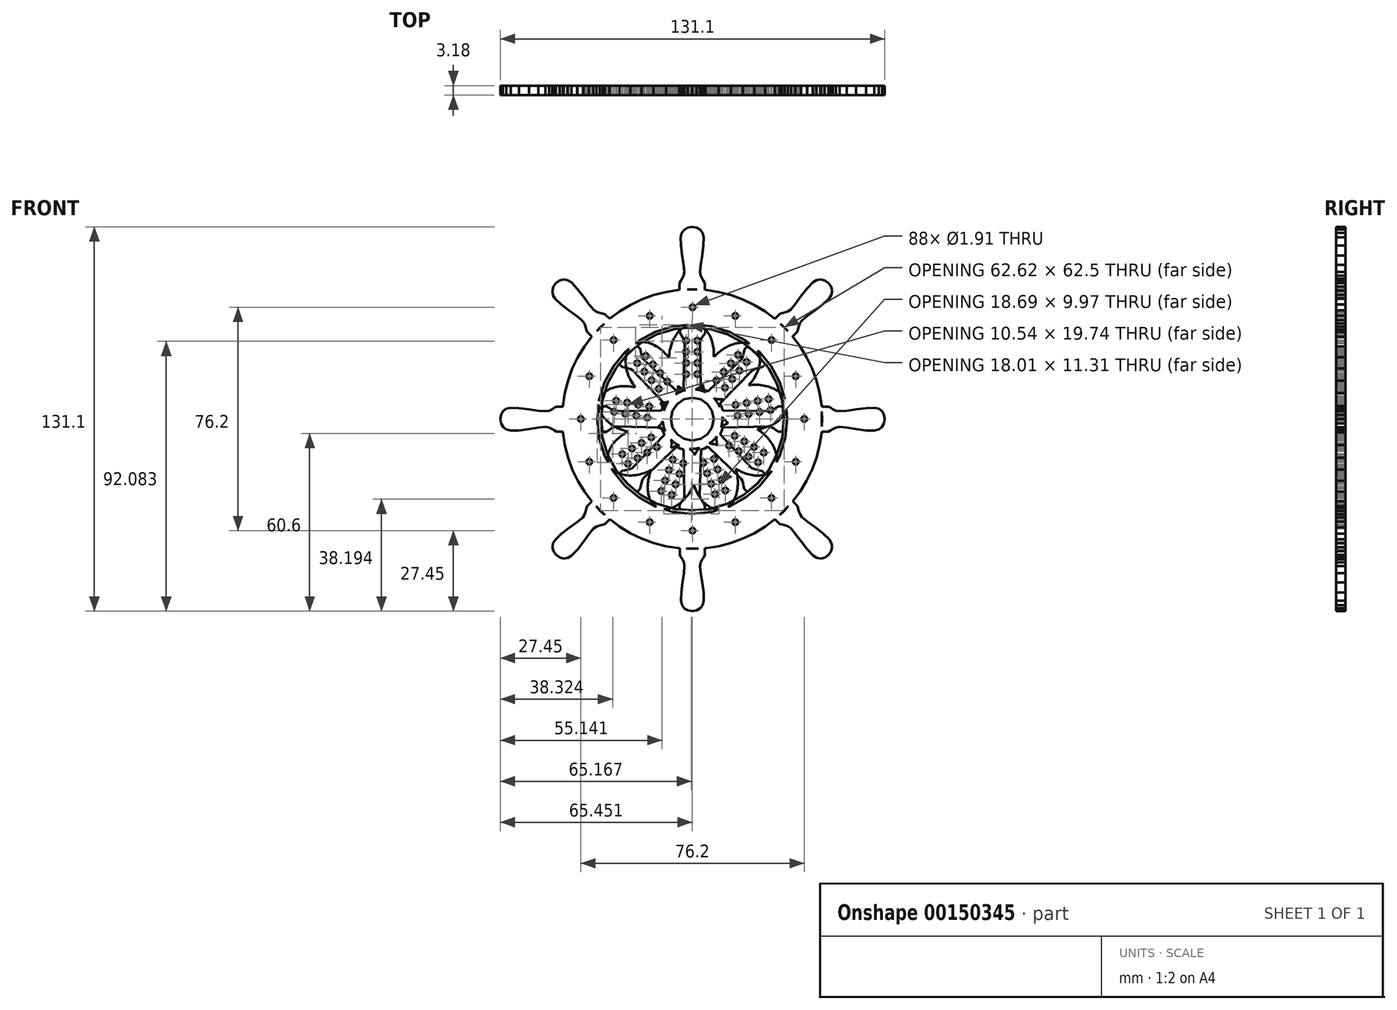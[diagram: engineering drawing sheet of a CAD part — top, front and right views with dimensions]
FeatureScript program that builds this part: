
annotation { "Feature Type Name" : "Feature", "Feature Type Description" : "" }
export const myFeature = defineFeature(function(context is Context, id is Id, definition is map)
    precondition{}
    {
        {
            var Q0;
            Q0=qCreatedBy(makeId("Front.planeOp"),FACE);
            var sketch = newSketch(context, id + "F0", { "sketchPlane" : qUnion([Q0])});
            skLineSegment(sketch, "E0", {"start": v(-9.65, -2.99) * mm, "end": v(-26.1, -2.56) * mm});
            skLineSegment(sketch, "E1", {"start": v(-26.1, -2.56) * mm, "end": v(-26.82, -2.77) * mm});
            skLineSegment(sketch, "E2", {"start": v(-26.82, -2.77) * mm, "end": v(-27.64, -3.22) * mm});
            skLineSegment(sketch, "E3", {"start": v(-27.64, -3.22) * mm, "end": v(-28.5, -3.78) * mm});
            skLineSegment(sketch, "E4", {"start": v(-28.5, -3.78) * mm, "end": v(-29.36, -4.29) * mm});
            skLineSegment(sketch, "E5", {"start": v(-29.36, -4.29) * mm, "end": v(-30.78, -4.29) * mm});
            skLineSegment(sketch, "E6", {"start": v(-30.78, -4.29) * mm, "end": v(-31.08, 0.04) * mm});
            skLineSegment(sketch, "E7", {"start": v(-31.08, 0.04) * mm, "end": v(-30.78, 4.37) * mm});
            skLineSegment(sketch, "E8", {"start": v(-30.78, 4.37) * mm, "end": v(-29.29, 4.37) * mm});
            skLineSegment(sketch, "E9", {"start": v(-29.29, 4.37) * mm, "end": v(-28.5, 3.85) * mm});
            skLineSegment(sketch, "E10", {"start": v(-28.5, 3.85) * mm, "end": v(-27.69, 3.29) * mm});
            skLineSegment(sketch, "E11", {"start": v(-27.69, 3.29) * mm, "end": v(-26.91, 2.84) * mm});
            skLineSegment(sketch, "E12", {"start": v(-26.91, 2.84) * mm, "end": v(-26.22, 2.67) * mm});
            skLineSegment(sketch, "E13", {"start": v(-26.22, 2.67) * mm, "end": v(-9.66, 2.93) * mm});
            skLineSegment(sketch, "E14", {"start": v(-29.33, -4.38) * mm, "end": v(-29.55, 0) * mm});
            skLineSegment(sketch, "E15", {"start": v(-29.55, 0) * mm, "end": v(-29.33, 4.44) * mm});
            skLineSegment(sketch, "E16", {"start": v(-62.02, -3.96) * mm, "end": v(-59.16, -3.9) * mm});
            skLineSegment(sketch, "E17", {"start": v(-59.16, -3.9) * mm, "end": v(-55.76, -3.45) * mm});
            skLineSegment(sketch, "E18", {"start": v(-55.76, -3.45) * mm, "end": v(-52.53, -2.95) * mm});
            skLineSegment(sketch, "E19", {"start": v(-52.53, -2.95) * mm, "end": v(-50.15, -2.7) * mm});
            skLineSegment(sketch, "E20", {"start": v(-50.15, -2.7) * mm, "end": v(-48.91, -2.92) * mm});
            skLineSegment(sketch, "E21", {"start": v(-48.91, -2.92) * mm, "end": v(-47.83, -3.44) * mm});
            skLineSegment(sketch, "E22", {"start": v(-47.83, -3.44) * mm, "end": v(-46.94, -3.98) * mm});
            skLineSegment(sketch, "E23", {"start": v(-46.94, -3.98) * mm, "end": v(-46.3, -4.31) * mm});
            skLineSegment(sketch, "E24", {"start": v(-46.3, -4.31) * mm, "end": v(-44.13, -4.33) * mm});
            skLineSegment(sketch, "E25", {"start": v(-44.13, -4.33) * mm, "end": v(-44.13, 4.25) * mm});
            skLineSegment(sketch, "E26", {"start": v(-44.13, 4.25) * mm, "end": v(-46.3, 4.23) * mm});
            skLineSegment(sketch, "E27", {"start": v(-46.3, 4.23) * mm, "end": v(-46.94, 3.9) * mm});
            skLineSegment(sketch, "E28", {"start": v(-46.94, 3.9) * mm, "end": v(-47.83, 3.36) * mm});
            skLineSegment(sketch, "E29", {"start": v(-47.83, 3.36) * mm, "end": v(-48.91, 2.85) * mm});
            skLineSegment(sketch, "E30", {"start": v(-48.91, 2.85) * mm, "end": v(-50.15, 2.62) * mm});
            skLineSegment(sketch, "E31", {"start": v(-50.15, 2.62) * mm, "end": v(-52.53, 2.85) * mm});
            skLineSegment(sketch, "E32", {"start": v(-52.53, 2.85) * mm, "end": v(-55.75, 3.32) * mm});
            skLineSegment(sketch, "E33", {"start": v(-55.75, 3.32) * mm, "end": v(-59.15, 3.75) * mm});
            skLineSegment(sketch, "E34", {"start": v(-59.15, 3.75) * mm, "end": v(-62.02, 3.87) * mm});
            skLineSegment(sketch, "E35", {"start": v(-62.02, 3.87) * mm, "end": v(-63.52, 3.5) * mm});
            skLineSegment(sketch, "E36", {"start": v(-63.52, 3.5) * mm, "end": v(-64.63, 2.66) * mm});
            skLineSegment(sketch, "E37", {"start": v(-64.63, 2.66) * mm, "end": v(-65.32, 1.44) * mm});
            skLineSegment(sketch, "E38", {"start": v(-65.32, 1.44) * mm, "end": v(-65.55, -0.04) * mm});
            skLineSegment(sketch, "E39", {"start": v(-65.55, -0.04) * mm, "end": v(-65.3, -1.56) * mm});
            skLineSegment(sketch, "E40", {"start": v(-65.3, -1.56) * mm, "end": v(-64.57, -2.76) * mm});
            skLineSegment(sketch, "E41", {"start": v(-64.57, -2.76) * mm, "end": v(-63.45, -3.57) * mm});
            skLineSegment(sketch, "E42", {"start": v(-63.45, -3.57) * mm, "end": v(-62.02, -3.96) * mm});
            skLineSegment(sketch, "E43", {"start": v(-46.16, -4.38) * mm, "end": v(-46.53, -0.02) * mm});
            skLineSegment(sketch, "E44", {"start": v(-46.53, -0.02) * mm, "end": v(-46.16, 4.33) * mm});
            skLineSegment(sketch, "E45", {"start": v(2.89, -9.76) * mm, "end": v(2.46, -26.18) * mm});
            skLineSegment(sketch, "E46", {"start": v(2.46, -26.18) * mm, "end": v(2.67, -26.9) * mm});
            skLineSegment(sketch, "E47", {"start": v(2.67, -26.9) * mm, "end": v(3.12, -27.72) * mm});
            skLineSegment(sketch, "E48", {"start": v(3.12, -27.72) * mm, "end": v(3.68, -28.58) * mm});
            skLineSegment(sketch, "E49", {"start": v(3.68, -28.58) * mm, "end": v(4.19, -29.44) * mm});
            skLineSegment(sketch, "E50", {"start": v(4.19, -29.44) * mm, "end": v(4.19, -30.85) * mm});
            skLineSegment(sketch, "E51", {"start": v(4.19, -30.85) * mm, "end": v(-0.15, -31.15) * mm});
            skLineSegment(sketch, "E52", {"start": v(-0.15, -31.15) * mm, "end": v(-4.49, -30.85) * mm});
            skLineSegment(sketch, "E53", {"start": v(-4.49, -30.85) * mm, "end": v(-4.49, -29.36) * mm});
            skLineSegment(sketch, "E54", {"start": v(-4.49, -29.36) * mm, "end": v(-3.97, -28.57) * mm});
            skLineSegment(sketch, "E55", {"start": v(-3.97, -28.57) * mm, "end": v(-3.4, -27.76) * mm});
            skLineSegment(sketch, "E56", {"start": v(-3.4, -27.76) * mm, "end": v(-2.96, -27) * mm});
            skLineSegment(sketch, "E57", {"start": v(-2.96, -27) * mm, "end": v(-2.79, -26.3) * mm});
            skLineSegment(sketch, "E58", {"start": v(-2.79, -26.3) * mm, "end": v(-3.05, -9.77) * mm});
            skLineSegment(sketch, "E59", {"start": v(4.28, -29.4) * mm, "end": v(-0.1, -29.62) * mm});
            skLineSegment(sketch, "E60", {"start": v(-0.1, -29.62) * mm, "end": v(-4.56, -29.4) * mm});
            skLineSegment(sketch, "E61", {"start": v(3.86, -62.02) * mm, "end": v(3.79, -59.17) * mm});
            skLineSegment(sketch, "E62", {"start": v(3.79, -59.17) * mm, "end": v(3.34, -55.78) * mm});
            skLineSegment(sketch, "E63", {"start": v(3.34, -55.78) * mm, "end": v(2.84, -52.55) * mm});
            skLineSegment(sketch, "E64", {"start": v(2.84, -52.55) * mm, "end": v(2.6, -50.18) * mm});
            skLineSegment(sketch, "E65", {"start": v(2.6, -50.18) * mm, "end": v(2.82, -48.95) * mm});
            skLineSegment(sketch, "E66", {"start": v(2.82, -48.95) * mm, "end": v(3.33, -47.86) * mm});
            skLineSegment(sketch, "E67", {"start": v(3.33, -47.86) * mm, "end": v(3.88, -46.98) * mm});
            skLineSegment(sketch, "E68", {"start": v(3.88, -46.98) * mm, "end": v(4.21, -46.34) * mm});
            skLineSegment(sketch, "E69", {"start": v(4.21, -46.34) * mm, "end": v(4.23, -44.17) * mm});
            skLineSegment(sketch, "E70", {"start": v(4.23, -44.17) * mm, "end": v(-4.37, -44.17) * mm});
            skLineSegment(sketch, "E71", {"start": v(-4.37, -44.17) * mm, "end": v(-4.35, -46.34) * mm});
            skLineSegment(sketch, "E72", {"start": v(-4.35, -46.34) * mm, "end": v(-4.02, -46.98) * mm});
            skLineSegment(sketch, "E73", {"start": v(-4.02, -46.98) * mm, "end": v(-3.48, -47.86) * mm});
            skLineSegment(sketch, "E74", {"start": v(-3.48, -47.86) * mm, "end": v(-2.96, -48.95) * mm});
            skLineSegment(sketch, "E75", {"start": v(-2.96, -48.95) * mm, "end": v(-2.74, -50.18) * mm});
            skLineSegment(sketch, "E76", {"start": v(-2.74, -50.18) * mm, "end": v(-2.97, -52.55) * mm});
            skLineSegment(sketch, "E77", {"start": v(-2.97, -52.55) * mm, "end": v(-3.44, -55.77) * mm});
            skLineSegment(sketch, "E78", {"start": v(-3.44, -55.77) * mm, "end": v(-3.87, -59.16) * mm});
            skLineSegment(sketch, "E79", {"start": v(-3.87, -59.16) * mm, "end": v(-3.99, -62.02) * mm});
            skLineSegment(sketch, "E80", {"start": v(-3.99, -62.02) * mm, "end": v(-3.62, -63.52) * mm});
            skLineSegment(sketch, "E81", {"start": v(-3.62, -63.52) * mm, "end": v(-2.77, -64.63) * mm});
            skLineSegment(sketch, "E82", {"start": v(-2.77, -64.63) * mm, "end": v(-1.55, -65.31) * mm});
            skLineSegment(sketch, "E83", {"start": v(-1.55, -65.31) * mm, "end": v(-0.07, -65.55) * mm});
            skLineSegment(sketch, "E84", {"start": v(-0.07, -65.55) * mm, "end": v(1.46, -65.3) * mm});
            skLineSegment(sketch, "E85", {"start": v(1.46, -65.3) * mm, "end": v(2.65, -64.57) * mm});
            skLineSegment(sketch, "E86", {"start": v(2.65, -64.57) * mm, "end": v(3.47, -63.46) * mm});
            skLineSegment(sketch, "E87", {"start": v(3.47, -63.46) * mm, "end": v(3.86, -62.02) * mm});
            skLineSegment(sketch, "E88", {"start": v(4.27, -46.2) * mm, "end": v(-0.09, -46.56) * mm});
            skLineSegment(sketch, "E89", {"start": v(-0.09, -46.56) * mm, "end": v(-4.45, -46.2) * mm});
            skLineSegment(sketch, "E90", {"start": v(-3.08, 9.76) * mm, "end": v(-2.66, 26.18) * mm});
            skLineSegment(sketch, "E91", {"start": v(-2.66, 26.18) * mm, "end": v(-2.86, 26.9) * mm});
            skLineSegment(sketch, "E92", {"start": v(-2.86, 26.9) * mm, "end": v(-3.32, 27.72) * mm});
            skLineSegment(sketch, "E93", {"start": v(-3.32, 27.72) * mm, "end": v(-3.88, 28.58) * mm});
            skLineSegment(sketch, "E94", {"start": v(-3.88, 28.58) * mm, "end": v(-4.38, 29.44) * mm});
            skLineSegment(sketch, "E95", {"start": v(-4.38, 29.44) * mm, "end": v(-4.38, 30.85) * mm});
            skLineSegment(sketch, "E96", {"start": v(-4.38, 30.85) * mm, "end": v(-0.05, 31.15) * mm});
            skLineSegment(sketch, "E97", {"start": v(-0.05, 31.15) * mm, "end": v(4.29, 30.85) * mm});
            skLineSegment(sketch, "E98", {"start": v(4.29, 30.85) * mm, "end": v(4.29, 29.36) * mm});
            skLineSegment(sketch, "E99", {"start": v(4.29, 29.36) * mm, "end": v(3.77, 28.57) * mm});
            skLineSegment(sketch, "E100", {"start": v(3.77, 28.57) * mm, "end": v(3.2, 27.76) * mm});
            skLineSegment(sketch, "E101", {"start": v(3.2, 27.76) * mm, "end": v(2.76, 27) * mm});
            skLineSegment(sketch, "E102", {"start": v(2.76, 27) * mm, "end": v(2.59, 26.3) * mm});
            skLineSegment(sketch, "E103", {"start": v(2.59, 26.3) * mm, "end": v(2.85, 9.77) * mm});
            skLineSegment(sketch, "E104", {"start": v(-4.48, 29.4) * mm, "end": v(-0.1, 29.62) * mm});
            skLineSegment(sketch, "E105", {"start": v(-0.1, 29.62) * mm, "end": v(4.36, 29.4) * mm});
            skLineSegment(sketch, "E106", {"start": v(-4.05, 62.02) * mm, "end": v(-3.99, 59.17) * mm});
            skLineSegment(sketch, "E107", {"start": v(-3.99, 59.17) * mm, "end": v(-3.54, 55.78) * mm});
            skLineSegment(sketch, "E108", {"start": v(-3.54, 55.78) * mm, "end": v(-3.04, 52.56) * mm});
            skLineSegment(sketch, "E109", {"start": v(-3.04, 52.56) * mm, "end": v(-2.8, 50.18) * mm});
            skLineSegment(sketch, "E110", {"start": v(-2.8, 50.18) * mm, "end": v(-3.02, 48.95) * mm});
            skLineSegment(sketch, "E111", {"start": v(-3.02, 48.95) * mm, "end": v(-3.53, 47.86) * mm});
            skLineSegment(sketch, "E112", {"start": v(-3.53, 47.86) * mm, "end": v(-4.08, 46.98) * mm});
            skLineSegment(sketch, "E113", {"start": v(-4.08, 46.98) * mm, "end": v(-4.4, 46.34) * mm});
            skLineSegment(sketch, "E114", {"start": v(-4.4, 46.34) * mm, "end": v(-4.43, 44.17) * mm});
            skLineSegment(sketch, "E115", {"start": v(-4.43, 44.17) * mm, "end": v(4.17, 44.17) * mm});
            skLineSegment(sketch, "E116", {"start": v(4.17, 44.17) * mm, "end": v(4.15, 46.34) * mm});
            skLineSegment(sketch, "E117", {"start": v(4.15, 46.34) * mm, "end": v(3.82, 46.98) * mm});
            skLineSegment(sketch, "E118", {"start": v(3.82, 46.98) * mm, "end": v(3.28, 47.86) * mm});
            skLineSegment(sketch, "E119", {"start": v(3.28, 47.86) * mm, "end": v(2.76, 48.95) * mm});
            skLineSegment(sketch, "E120", {"start": v(2.76, 48.95) * mm, "end": v(2.54, 50.18) * mm});
            skLineSegment(sketch, "E121", {"start": v(2.54, 50.18) * mm, "end": v(2.77, 52.55) * mm});
            skLineSegment(sketch, "E122", {"start": v(2.77, 52.55) * mm, "end": v(3.24, 55.77) * mm});
            skLineSegment(sketch, "E123", {"start": v(3.24, 55.77) * mm, "end": v(3.67, 59.16) * mm});
            skLineSegment(sketch, "E124", {"start": v(3.67, 59.16) * mm, "end": v(3.8, 62.02) * mm});
            skLineSegment(sketch, "E125", {"start": v(3.8, 62.02) * mm, "end": v(3.42, 63.52) * mm});
            skLineSegment(sketch, "E126", {"start": v(3.42, 63.52) * mm, "end": v(2.57, 64.63) * mm});
            skLineSegment(sketch, "E127", {"start": v(2.57, 64.63) * mm, "end": v(1.35, 65.32) * mm});
            skLineSegment(sketch, "E128", {"start": v(1.35, 65.32) * mm, "end": v(-0.13, 65.55) * mm});
            skLineSegment(sketch, "E129", {"start": v(-0.13, 65.55) * mm, "end": v(-1.65, 65.3) * mm});
            skLineSegment(sketch, "E130", {"start": v(-1.65, 65.3) * mm, "end": v(-2.85, 64.57) * mm});
            skLineSegment(sketch, "E131", {"start": v(-2.85, 64.57) * mm, "end": v(-3.67, 63.46) * mm});
            skLineSegment(sketch, "E132", {"start": v(-3.67, 63.46) * mm, "end": v(-4.05, 62.02) * mm});
            skLineSegment(sketch, "E133", {"start": v(-4.47, 46.2) * mm, "end": v(-0.11, 46.57) * mm});
            skLineSegment(sketch, "E134", {"start": v(-0.11, 46.57) * mm, "end": v(4.25, 46.2) * mm});
            skLineSegment(sketch, "E135", {"start": v(8.93, -4.8) * mm, "end": v(20.26, -16.7) * mm});
            skLineSegment(sketch, "E136", {"start": v(20.26, -16.7) * mm, "end": v(20.92, -17.07) * mm});
            skLineSegment(sketch, "E137", {"start": v(20.92, -17.07) * mm, "end": v(21.82, -17.33) * mm});
            skLineSegment(sketch, "E138", {"start": v(21.82, -17.33) * mm, "end": v(22.82, -17.54) * mm});
            skLineSegment(sketch, "E139", {"start": v(22.82, -17.54) * mm, "end": v(23.79, -17.8) * mm});
            skLineSegment(sketch, "E140", {"start": v(23.79, -17.8) * mm, "end": v(24.79, -18.79) * mm});
            skLineSegment(sketch, "E141", {"start": v(24.79, -18.79) * mm, "end": v(21.94, -22.07) * mm});
            skLineSegment(sketch, "E142", {"start": v(21.94, -22.07) * mm, "end": v(18.65, -24.9) * mm});
            skLineSegment(sketch, "E143", {"start": v(18.65, -24.9) * mm, "end": v(17.6, -23.86) * mm});
            skLineSegment(sketch, "E144", {"start": v(17.6, -23.86) * mm, "end": v(17.4, -22.93) * mm});
            skLineSegment(sketch, "E145", {"start": v(17.4, -22.93) * mm, "end": v(17.24, -21.96) * mm});
            skLineSegment(sketch, "E146", {"start": v(17.24, -21.96) * mm, "end": v(17, -21.1) * mm});
            skLineSegment(sketch, "E147", {"start": v(17, -21.1) * mm, "end": v(16.63, -20.5) * mm});
            skLineSegment(sketch, "E148", {"start": v(16.63, -20.5) * mm, "end": v(4.74, -9) * mm});
            skLineSegment(sketch, "E149", {"start": v(23.83, -17.7) * mm, "end": v(20.88, -20.95) * mm});
            skLineSegment(sketch, "E150", {"start": v(20.88, -20.95) * mm, "end": v(17.58, -23.94) * mm});
            skLineSegment(sketch, "E151", {"start": v(46.64, -41.07) * mm, "end": v(44.57, -39.1) * mm});
            skLineSegment(sketch, "E152", {"start": v(44.57, -39.1) * mm, "end": v(41.86, -37.01) * mm});
            skLineSegment(sketch, "E153", {"start": v(41.86, -37.01) * mm, "end": v(39.22, -35.08) * mm});
            skLineSegment(sketch, "E154", {"start": v(39.22, -35.08) * mm, "end": v(37.36, -33.58) * mm});
            skLineSegment(sketch, "E155", {"start": v(37.36, -33.58) * mm, "end": v(36.65, -32.55) * mm});
            skLineSegment(sketch, "E156", {"start": v(36.65, -32.55) * mm, "end": v(36.24, -31.42) * mm});
            skLineSegment(sketch, "E157", {"start": v(36.24, -31.42) * mm, "end": v(36, -30.4) * mm});
            skLineSegment(sketch, "E158", {"start": v(36, -30.4) * mm, "end": v(35.78, -29.73) * mm});
            skLineSegment(sketch, "E159", {"start": v(35.78, -29.73) * mm, "end": v(34.26, -28.18) * mm});
            skLineSegment(sketch, "E160", {"start": v(34.26, -28.18) * mm, "end": v(28.18, -34.25) * mm});
            skLineSegment(sketch, "E161", {"start": v(28.18, -34.25) * mm, "end": v(29.73, -35.77) * mm});
            skLineSegment(sketch, "E162", {"start": v(29.73, -35.77) * mm, "end": v(30.41, -35.99) * mm});
            skLineSegment(sketch, "E163", {"start": v(30.41, -35.99) * mm, "end": v(31.43, -36.23) * mm});
            skLineSegment(sketch, "E164", {"start": v(31.43, -36.23) * mm, "end": v(32.56, -36.63) * mm});
            skLineSegment(sketch, "E165", {"start": v(32.56, -36.63) * mm, "end": v(33.59, -37.35) * mm});
            skLineSegment(sketch, "E166", {"start": v(33.59, -37.35) * mm, "end": v(35.1, -39.18) * mm});
            skLineSegment(sketch, "E167", {"start": v(35.1, -39.18) * mm, "end": v(37.06, -41.8) * mm});
            skLineSegment(sketch, "E168", {"start": v(37.06, -41.8) * mm, "end": v(39.15, -44.5) * mm});
            skLineSegment(sketch, "E169", {"start": v(39.15, -44.5) * mm, "end": v(41.1, -46.6) * mm});
            skLineSegment(sketch, "E170", {"start": v(41.1, -46.6) * mm, "end": v(42.42, -47.4) * mm});
            skLineSegment(sketch, "E171", {"start": v(42.42, -47.4) * mm, "end": v(43.8, -47.58) * mm});
            skLineSegment(sketch, "E172", {"start": v(43.8, -47.58) * mm, "end": v(45.15, -47.2) * mm});
            skLineSegment(sketch, "E173", {"start": v(45.15, -47.2) * mm, "end": v(46.37, -46.33) * mm});
            skLineSegment(sketch, "E174", {"start": v(46.37, -46.33) * mm, "end": v(47.26, -45.07) * mm});
            skLineSegment(sketch, "E175", {"start": v(47.26, -45.07) * mm, "end": v(47.6, -43.72) * mm});
            skLineSegment(sketch, "E176", {"start": v(47.6, -43.72) * mm, "end": v(47.39, -42.35) * mm});
            skLineSegment(sketch, "E177", {"start": v(47.39, -42.35) * mm, "end": v(46.64, -41.07) * mm});
            skLineSegment(sketch, "E178", {"start": v(35.73, -29.58) * mm, "end": v(32.9, -32.92) * mm});
            skLineSegment(sketch, "E179", {"start": v(32.9, -32.92) * mm, "end": v(29.56, -35.74) * mm});
            skLineSegment(sketch, "E180", {"start": v(-9.13, 4.8) * mm, "end": v(-20.46, 16.7) * mm});
            skLineSegment(sketch, "E181", {"start": v(-20.46, 16.7) * mm, "end": v(-21.12, 17.07) * mm});
            skLineSegment(sketch, "E182", {"start": v(-21.12, 17.07) * mm, "end": v(-22.02, 17.33) * mm});
            skLineSegment(sketch, "E183", {"start": v(-22.02, 17.33) * mm, "end": v(-23.02, 17.55) * mm});
            skLineSegment(sketch, "E184", {"start": v(-23.02, 17.55) * mm, "end": v(-23.98, 17.8) * mm});
            skLineSegment(sketch, "E185", {"start": v(-23.98, 17.8) * mm, "end": v(-24.98, 18.79) * mm});
            skLineSegment(sketch, "E186", {"start": v(-24.98, 18.79) * mm, "end": v(-22.14, 22.07) * mm});
            skLineSegment(sketch, "E187", {"start": v(-22.14, 22.07) * mm, "end": v(-18.85, 24.9) * mm});
            skLineSegment(sketch, "E188", {"start": v(-18.85, 24.9) * mm, "end": v(-17.8, 23.86) * mm});
            skLineSegment(sketch, "E189", {"start": v(-17.8, 23.86) * mm, "end": v(-17.6, 22.93) * mm});
            skLineSegment(sketch, "E190", {"start": v(-17.6, 22.93) * mm, "end": v(-17.43, 21.97) * mm});
            skLineSegment(sketch, "E191", {"start": v(-17.43, 21.97) * mm, "end": v(-17.2, 21.1) * mm});
            skLineSegment(sketch, "E192", {"start": v(-17.2, 21.1) * mm, "end": v(-16.83, 20.5) * mm});
            skLineSegment(sketch, "E193", {"start": v(-16.83, 20.5) * mm, "end": v(-4.94, 9) * mm});
            skLineSegment(sketch, "E194", {"start": v(-24.03, 17.7) * mm, "end": v(-21.08, 20.95) * mm});
            skLineSegment(sketch, "E195", {"start": v(-21.08, 20.95) * mm, "end": v(-17.78, 23.94) * mm});
            skLineSegment(sketch, "E196", {"start": v(-46.84, 41.07) * mm, "end": v(-44.77, 39.1) * mm});
            skLineSegment(sketch, "E197", {"start": v(-44.77, 39.1) * mm, "end": v(-42.06, 37.01) * mm});
            skLineSegment(sketch, "E198", {"start": v(-42.06, 37.01) * mm, "end": v(-39.42, 35.09) * mm});
            skLineSegment(sketch, "E199", {"start": v(-39.42, 35.09) * mm, "end": v(-37.56, 33.58) * mm});
            skLineSegment(sketch, "E200", {"start": v(-37.56, 33.58) * mm, "end": v(-36.84, 32.55) * mm});
            skLineSegment(sketch, "E201", {"start": v(-36.84, 32.55) * mm, "end": v(-36.44, 31.42) * mm});
            skLineSegment(sketch, "E202", {"start": v(-36.44, 31.42) * mm, "end": v(-36.2, 30.4) * mm});
            skLineSegment(sketch, "E203", {"start": v(-36.2, 30.4) * mm, "end": v(-35.98, 29.73) * mm});
            skLineSegment(sketch, "E204", {"start": v(-35.98, 29.73) * mm, "end": v(-34.45, 28.18) * mm});
            skLineSegment(sketch, "E205", {"start": v(-34.45, 28.18) * mm, "end": v(-28.38, 34.25) * mm});
            skLineSegment(sketch, "E206", {"start": v(-28.38, 34.25) * mm, "end": v(-29.93, 35.77) * mm});
            skLineSegment(sketch, "E207", {"start": v(-29.93, 35.77) * mm, "end": v(-30.61, 35.99) * mm});
            skLineSegment(sketch, "E208", {"start": v(-30.61, 35.99) * mm, "end": v(-31.62, 36.23) * mm});
            skLineSegment(sketch, "E209", {"start": v(-31.62, 36.23) * mm, "end": v(-32.76, 36.63) * mm});
            skLineSegment(sketch, "E210", {"start": v(-32.76, 36.63) * mm, "end": v(-33.79, 37.35) * mm});
            skLineSegment(sketch, "E211", {"start": v(-33.79, 37.35) * mm, "end": v(-35.3, 39.18) * mm});
            skLineSegment(sketch, "E212", {"start": v(-35.3, 39.18) * mm, "end": v(-37.26, 41.8) * mm});
            skLineSegment(sketch, "E213", {"start": v(-37.26, 41.8) * mm, "end": v(-39.35, 44.5) * mm});
            skLineSegment(sketch, "E214", {"start": v(-39.35, 44.5) * mm, "end": v(-41.3, 46.6) * mm});
            skLineSegment(sketch, "E215", {"start": v(-41.3, 46.6) * mm, "end": v(-42.62, 47.4) * mm});
            skLineSegment(sketch, "E216", {"start": v(-42.62, 47.4) * mm, "end": v(-44, 47.59) * mm});
            skLineSegment(sketch, "E217", {"start": v(-44, 47.59) * mm, "end": v(-45.35, 47.21) * mm});
            skLineSegment(sketch, "E218", {"start": v(-45.35, 47.21) * mm, "end": v(-46.57, 46.33) * mm});
            skLineSegment(sketch, "E219", {"start": v(-46.57, 46.33) * mm, "end": v(-47.46, 45.07) * mm});
            skLineSegment(sketch, "E220", {"start": v(-47.46, 45.07) * mm, "end": v(-47.8, 43.72) * mm});
            skLineSegment(sketch, "E221", {"start": v(-47.8, 43.72) * mm, "end": v(-47.58, 42.35) * mm});
            skLineSegment(sketch, "E222", {"start": v(-47.58, 42.35) * mm, "end": v(-46.84, 41.07) * mm});
            skLineSegment(sketch, "E223", {"start": v(-35.92, 29.58) * mm, "end": v(-33.1, 32.92) * mm});
            skLineSegment(sketch, "E224", {"start": v(-33.1, 32.92) * mm, "end": v(-29.76, 35.74) * mm});
            skLineSegment(sketch, "E225", {"start": v(-4.9, -9) * mm, "end": v(-16.84, -20.32) * mm});
            skLineSegment(sketch, "E226", {"start": v(-16.84, -20.32) * mm, "end": v(-17.2, -20.97) * mm});
            skLineSegment(sketch, "E227", {"start": v(-17.2, -20.97) * mm, "end": v(-17.46, -21.87) * mm});
            skLineSegment(sketch, "E228", {"start": v(-17.46, -21.87) * mm, "end": v(-17.68, -22.88) * mm});
            skLineSegment(sketch, "E229", {"start": v(-17.68, -22.88) * mm, "end": v(-17.93, -23.84) * mm});
            skLineSegment(sketch, "E230", {"start": v(-17.93, -23.84) * mm, "end": v(-18.93, -24.83) * mm});
            skLineSegment(sketch, "E231", {"start": v(-18.93, -24.83) * mm, "end": v(-22.2, -22) * mm});
            skLineSegment(sketch, "E232", {"start": v(-22.2, -22) * mm, "end": v(-25.06, -18.72) * mm});
            skLineSegment(sketch, "E233", {"start": v(-25.06, -18.72) * mm, "end": v(-24, -17.66) * mm});
            skLineSegment(sketch, "E234", {"start": v(-24, -17.66) * mm, "end": v(-23.08, -17.47) * mm});
            skLineSegment(sketch, "E235", {"start": v(-23.08, -17.47) * mm, "end": v(-22.1, -17.3) * mm});
            skLineSegment(sketch, "E236", {"start": v(-22.1, -17.3) * mm, "end": v(-21.24, -17.07) * mm});
            skLineSegment(sketch, "E237", {"start": v(-21.24, -17.07) * mm, "end": v(-20.63, -16.7) * mm});
            skLineSegment(sketch, "E238", {"start": v(-20.63, -16.7) * mm, "end": v(-9.1, -4.83) * mm});
            skLineSegment(sketch, "E239", {"start": v(-17.84, -23.88) * mm, "end": v(-21.09, -20.94) * mm});
            skLineSegment(sketch, "E240", {"start": v(-21.09, -20.94) * mm, "end": v(-24.09, -17.65) * mm});
            skLineSegment(sketch, "E241", {"start": v(-41.25, -46.65) * mm, "end": v(-39.27, -44.58) * mm});
            skLineSegment(sketch, "E242", {"start": v(-39.27, -44.58) * mm, "end": v(-37.19, -41.87) * mm});
            skLineSegment(sketch, "E243", {"start": v(-37.19, -41.87) * mm, "end": v(-35.26, -39.24) * mm});
            skLineSegment(sketch, "E244", {"start": v(-35.26, -39.24) * mm, "end": v(-33.75, -37.39) * mm});
            skLineSegment(sketch, "E245", {"start": v(-33.75, -37.39) * mm, "end": v(-32.72, -36.67) * mm});
            skLineSegment(sketch, "E246", {"start": v(-32.72, -36.67) * mm, "end": v(-31.58, -36.27) * mm});
            skLineSegment(sketch, "E247", {"start": v(-31.58, -36.27) * mm, "end": v(-30.57, -36.03) * mm});
            skLineSegment(sketch, "E248", {"start": v(-30.57, -36.03) * mm, "end": v(-29.89, -35.81) * mm});
            skLineSegment(sketch, "E249", {"start": v(-29.89, -35.81) * mm, "end": v(-28.34, -34.29) * mm});
            skLineSegment(sketch, "E250", {"start": v(-28.34, -34.29) * mm, "end": v(-34.41, -28.22) * mm});
            skLineSegment(sketch, "E251", {"start": v(-34.41, -28.22) * mm, "end": v(-35.94, -29.77) * mm});
            skLineSegment(sketch, "E252", {"start": v(-35.94, -29.77) * mm, "end": v(-36.16, -30.45) * mm});
            skLineSegment(sketch, "E253", {"start": v(-36.16, -30.45) * mm, "end": v(-36.4, -31.46) * mm});
            skLineSegment(sketch, "E254", {"start": v(-36.4, -31.46) * mm, "end": v(-36.8, -32.6) * mm});
            skLineSegment(sketch, "E255", {"start": v(-36.8, -32.6) * mm, "end": v(-37.52, -33.62) * mm});
            skLineSegment(sketch, "E256", {"start": v(-37.52, -33.62) * mm, "end": v(-39.36, -35.14) * mm});
            skLineSegment(sketch, "E257", {"start": v(-39.36, -35.14) * mm, "end": v(-41.97, -37.08) * mm});
            skLineSegment(sketch, "E258", {"start": v(-41.97, -37.08) * mm, "end": v(-44.68, -39.17) * mm});
            skLineSegment(sketch, "E259", {"start": v(-44.68, -39.17) * mm, "end": v(-46.8, -41.11) * mm});
            skLineSegment(sketch, "E260", {"start": v(-46.8, -41.11) * mm, "end": v(-47.6, -42.43) * mm});
            skLineSegment(sketch, "E261", {"start": v(-47.6, -42.43) * mm, "end": v(-47.78, -43.81) * mm});
            skLineSegment(sketch, "E262", {"start": v(-47.78, -43.81) * mm, "end": v(-47.4, -45.16) * mm});
            skLineSegment(sketch, "E263", {"start": v(-47.4, -45.16) * mm, "end": v(-46.52, -46.37) * mm});
            skLineSegment(sketch, "E264", {"start": v(-46.52, -46.37) * mm, "end": v(-45.26, -47.27) * mm});
            skLineSegment(sketch, "E265", {"start": v(-45.26, -47.27) * mm, "end": v(-43.9, -47.6) * mm});
            skLineSegment(sketch, "E266", {"start": v(-43.9, -47.6) * mm, "end": v(-42.54, -47.39) * mm});
            skLineSegment(sketch, "E267", {"start": v(-42.54, -47.39) * mm, "end": v(-41.25, -46.65) * mm});
            skLineSegment(sketch, "E268", {"start": v(-29.74, -35.75) * mm, "end": v(-33.08, -32.93) * mm});
            skLineSegment(sketch, "E269", {"start": v(-33.08, -32.93) * mm, "end": v(-35.9, -29.6) * mm});
            skLineSegment(sketch, "E270", {"start": v(4.7, 9) * mm, "end": v(16.64, 20.32) * mm});
            skLineSegment(sketch, "E271", {"start": v(16.64, 20.32) * mm, "end": v(17, 20.97) * mm});
            skLineSegment(sketch, "E272", {"start": v(17, 20.97) * mm, "end": v(17.26, 21.88) * mm});
            skLineSegment(sketch, "E273", {"start": v(17.26, 21.88) * mm, "end": v(17.48, 22.88) * mm});
            skLineSegment(sketch, "E274", {"start": v(17.48, 22.88) * mm, "end": v(17.73, 23.84) * mm});
            skLineSegment(sketch, "E275", {"start": v(17.73, 23.84) * mm, "end": v(18.73, 24.84) * mm});
            skLineSegment(sketch, "E276", {"start": v(18.73, 24.84) * mm, "end": v(22.01, 22) * mm});
            skLineSegment(sketch, "E277", {"start": v(22.01, 22) * mm, "end": v(24.86, 18.72) * mm});
            skLineSegment(sketch, "E278", {"start": v(24.86, 18.72) * mm, "end": v(23.8, 17.66) * mm});
            skLineSegment(sketch, "E279", {"start": v(23.8, 17.66) * mm, "end": v(22.88, 17.47) * mm});
            skLineSegment(sketch, "E280", {"start": v(22.88, 17.47) * mm, "end": v(21.9, 17.3) * mm});
            skLineSegment(sketch, "E281", {"start": v(21.9, 17.3) * mm, "end": v(21.04, 17.07) * mm});
            skLineSegment(sketch, "E282", {"start": v(21.04, 17.07) * mm, "end": v(20.43, 16.7) * mm});
            skLineSegment(sketch, "E283", {"start": v(20.43, 16.7) * mm, "end": v(8.91, 4.83) * mm});
            skLineSegment(sketch, "E284", {"start": v(17.64, 23.88) * mm, "end": v(20.89, 20.94) * mm});
            skLineSegment(sketch, "E285", {"start": v(20.89, 20.94) * mm, "end": v(23.9, 17.65) * mm});
            skLineSegment(sketch, "E286", {"start": v(41.05, 46.65) * mm, "end": v(39.07, 44.58) * mm});
            skLineSegment(sketch, "E287", {"start": v(39.07, 44.58) * mm, "end": v(36.99, 41.87) * mm});
            skLineSegment(sketch, "E288", {"start": v(36.99, 41.87) * mm, "end": v(35.06, 39.24) * mm});
            skLineSegment(sketch, "E289", {"start": v(35.06, 39.24) * mm, "end": v(33.55, 37.39) * mm});
            skLineSegment(sketch, "E290", {"start": v(33.55, 37.39) * mm, "end": v(32.52, 36.67) * mm});
            skLineSegment(sketch, "E291", {"start": v(32.52, 36.67) * mm, "end": v(31.39, 36.27) * mm});
            skLineSegment(sketch, "E292", {"start": v(31.39, 36.27) * mm, "end": v(30.37, 36.03) * mm});
            skLineSegment(sketch, "E293", {"start": v(30.37, 36.03) * mm, "end": v(29.69, 35.81) * mm});
            skLineSegment(sketch, "E294", {"start": v(29.69, 35.81) * mm, "end": v(28.14, 34.29) * mm});
            skLineSegment(sketch, "E295", {"start": v(28.14, 34.29) * mm, "end": v(34.22, 28.22) * mm});
            skLineSegment(sketch, "E296", {"start": v(34.22, 28.22) * mm, "end": v(35.74, 29.77) * mm});
            skLineSegment(sketch, "E297", {"start": v(35.74, 29.77) * mm, "end": v(35.96, 30.45) * mm});
            skLineSegment(sketch, "E298", {"start": v(35.96, 30.45) * mm, "end": v(36.2, 31.46) * mm});
            skLineSegment(sketch, "E299", {"start": v(36.2, 31.46) * mm, "end": v(36.6, 32.6) * mm});
            skLineSegment(sketch, "E300", {"start": v(36.6, 32.6) * mm, "end": v(37.32, 33.62) * mm});
            skLineSegment(sketch, "E301", {"start": v(37.32, 33.62) * mm, "end": v(39.16, 35.14) * mm});
            skLineSegment(sketch, "E302", {"start": v(39.16, 35.14) * mm, "end": v(41.78, 37.08) * mm});
            skLineSegment(sketch, "E303", {"start": v(41.78, 37.08) * mm, "end": v(44.48, 39.17) * mm});
            skLineSegment(sketch, "E304", {"start": v(44.48, 39.17) * mm, "end": v(46.6, 41.11) * mm});
            skLineSegment(sketch, "E305", {"start": v(46.6, 41.11) * mm, "end": v(47.4, 42.44) * mm});
            skLineSegment(sketch, "E306", {"start": v(47.4, 42.44) * mm, "end": v(47.58, 43.82) * mm});
            skLineSegment(sketch, "E307", {"start": v(47.58, 43.82) * mm, "end": v(47.2, 45.16) * mm});
            skLineSegment(sketch, "E308", {"start": v(47.2, 45.16) * mm, "end": v(46.32, 46.37) * mm});
            skLineSegment(sketch, "E309", {"start": v(46.32, 46.37) * mm, "end": v(45.06, 47.27) * mm});
            skLineSegment(sketch, "E310", {"start": v(45.06, 47.27) * mm, "end": v(43.7, 47.6) * mm});
            skLineSegment(sketch, "E311", {"start": v(43.7, 47.6) * mm, "end": v(42.34, 47.4) * mm});
            skLineSegment(sketch, "E312", {"start": v(42.34, 47.4) * mm, "end": v(41.05, 46.65) * mm});
            skLineSegment(sketch, "E313", {"start": v(29.54, 35.75) * mm, "end": v(32.88, 32.94) * mm});
            skLineSegment(sketch, "E314", {"start": v(32.88, 32.94) * mm, "end": v(35.7, 29.6) * mm});
            skLineSegment(sketch, "E315", {"start": v(3.54, -0.01) * mm, "end": v(3.25, -1.42) * mm});
            skLineSegment(sketch, "E316", {"start": v(3.25, -1.42) * mm, "end": v(2.47, -2.58) * mm});
            skLineSegment(sketch, "E317", {"start": v(2.47, -2.58) * mm, "end": v(1.32, -3.36) * mm});
            skLineSegment(sketch, "E318", {"start": v(1.32, -3.36) * mm, "end": v(-0.1, -3.64) * mm});
            skLineSegment(sketch, "E319", {"start": v(-0.1, -3.64) * mm, "end": v(-1.52, -3.36) * mm});
            skLineSegment(sketch, "E320", {"start": v(-1.52, -3.36) * mm, "end": v(-2.67, -2.58) * mm});
            skLineSegment(sketch, "E321", {"start": v(-2.67, -2.58) * mm, "end": v(-3.45, -1.42) * mm});
            skLineSegment(sketch, "E322", {"start": v(-3.45, -1.42) * mm, "end": v(-3.74, -0.01) * mm});
            skLineSegment(sketch, "E323", {"start": v(-3.74, -0.01) * mm, "end": v(-3.45, 1.4) * mm});
            skLineSegment(sketch, "E324", {"start": v(-3.45, 1.4) * mm, "end": v(-2.67, 2.56) * mm});
            skLineSegment(sketch, "E325", {"start": v(-2.67, 2.56) * mm, "end": v(-1.52, 3.33) * mm});
            skLineSegment(sketch, "E326", {"start": v(-1.52, 3.33) * mm, "end": v(-0.1, 3.62) * mm});
            skLineSegment(sketch, "E327", {"start": v(-0.1, 3.62) * mm, "end": v(1.32, 3.33) * mm});
            skLineSegment(sketch, "E328", {"start": v(1.32, 3.33) * mm, "end": v(2.47, 2.56) * mm});
            skLineSegment(sketch, "E329", {"start": v(2.47, 2.56) * mm, "end": v(3.25, 1.4) * mm});
            skLineSegment(sketch, "E330", {"start": v(3.25, 1.4) * mm, "end": v(3.54, -0.01) * mm});
            skLineSegment(sketch, "E331", {"start": v(9.65, -2.99) * mm, "end": v(26.1, -2.56) * mm});
            skLineSegment(sketch, "E332", {"start": v(26.1, -2.56) * mm, "end": v(26.82, -2.77) * mm});
            skLineSegment(sketch, "E333", {"start": v(26.82, -2.77) * mm, "end": v(27.64, -3.22) * mm});
            skLineSegment(sketch, "E334", {"start": v(27.64, -3.22) * mm, "end": v(28.5, -3.78) * mm});
            skLineSegment(sketch, "E335", {"start": v(28.5, -3.78) * mm, "end": v(29.36, -4.29) * mm});
            skLineSegment(sketch, "E336", {"start": v(29.36, -4.29) * mm, "end": v(30.78, -4.29) * mm});
            skLineSegment(sketch, "E337", {"start": v(30.78, -4.29) * mm, "end": v(31.08, 0.04) * mm});
            skLineSegment(sketch, "E338", {"start": v(31.08, 0.04) * mm, "end": v(30.78, 4.37) * mm});
            skLineSegment(sketch, "E339", {"start": v(30.78, 4.37) * mm, "end": v(29.29, 4.37) * mm});
            skLineSegment(sketch, "E340", {"start": v(29.29, 4.37) * mm, "end": v(28.5, 3.85) * mm});
            skLineSegment(sketch, "E341", {"start": v(28.5, 3.85) * mm, "end": v(27.69, 3.29) * mm});
            skLineSegment(sketch, "E342", {"start": v(27.69, 3.29) * mm, "end": v(26.91, 2.84) * mm});
            skLineSegment(sketch, "E343", {"start": v(26.91, 2.84) * mm, "end": v(26.22, 2.67) * mm});
            skLineSegment(sketch, "E344", {"start": v(26.22, 2.67) * mm, "end": v(9.66, 2.93) * mm});
            skLineSegment(sketch, "E345", {"start": v(29.33, -4.38) * mm, "end": v(29.55, 0) * mm});
            skLineSegment(sketch, "E346", {"start": v(29.55, 0) * mm, "end": v(29.33, 4.44) * mm});
            skLineSegment(sketch, "E347", {"start": v(62.02, -3.96) * mm, "end": v(59.16, -3.9) * mm});
            skLineSegment(sketch, "E348", {"start": v(59.16, -3.9) * mm, "end": v(55.76, -3.45) * mm});
            skLineSegment(sketch, "E349", {"start": v(55.76, -3.45) * mm, "end": v(52.53, -2.95) * mm});
            skLineSegment(sketch, "E350", {"start": v(52.53, -2.95) * mm, "end": v(50.15, -2.7) * mm});
            skLineSegment(sketch, "E351", {"start": v(50.15, -2.7) * mm, "end": v(48.91, -2.92) * mm});
            skLineSegment(sketch, "E352", {"start": v(48.91, -2.92) * mm, "end": v(47.83, -3.44) * mm});
            skLineSegment(sketch, "E353", {"start": v(47.83, -3.44) * mm, "end": v(46.94, -3.98) * mm});
            skLineSegment(sketch, "E354", {"start": v(46.94, -3.98) * mm, "end": v(46.3, -4.31) * mm});
            skLineSegment(sketch, "E355", {"start": v(46.3, -4.31) * mm, "end": v(44.13, -4.33) * mm});
            skLineSegment(sketch, "E356", {"start": v(44.13, -4.33) * mm, "end": v(44.13, 4.25) * mm});
            skLineSegment(sketch, "E357", {"start": v(44.13, 4.25) * mm, "end": v(46.3, 4.23) * mm});
            skLineSegment(sketch, "E358", {"start": v(46.3, 4.23) * mm, "end": v(46.94, 3.9) * mm});
            skLineSegment(sketch, "E359", {"start": v(46.94, 3.9) * mm, "end": v(47.83, 3.36) * mm});
            skLineSegment(sketch, "E360", {"start": v(47.83, 3.36) * mm, "end": v(48.91, 2.85) * mm});
            skLineSegment(sketch, "E361", {"start": v(48.91, 2.85) * mm, "end": v(50.15, 2.62) * mm});
            skLineSegment(sketch, "E362", {"start": v(50.15, 2.62) * mm, "end": v(52.52, 2.85) * mm});
            skLineSegment(sketch, "E363", {"start": v(52.52, 2.85) * mm, "end": v(55.75, 3.32) * mm});
            skLineSegment(sketch, "E364", {"start": v(55.75, 3.32) * mm, "end": v(59.14, 3.75) * mm});
            skLineSegment(sketch, "E365", {"start": v(59.14, 3.75) * mm, "end": v(62.02, 3.87) * mm});
            skLineSegment(sketch, "E366", {"start": v(62.02, 3.87) * mm, "end": v(63.52, 3.5) * mm});
            skLineSegment(sketch, "E367", {"start": v(63.52, 3.5) * mm, "end": v(64.63, 2.66) * mm});
            skLineSegment(sketch, "E368", {"start": v(64.63, 2.66) * mm, "end": v(65.31, 1.44) * mm});
            skLineSegment(sketch, "E369", {"start": v(65.31, 1.44) * mm, "end": v(65.55, -0.04) * mm});
            skLineSegment(sketch, "E370", {"start": v(65.55, -0.04) * mm, "end": v(65.3, -1.56) * mm});
            skLineSegment(sketch, "E371", {"start": v(65.3, -1.56) * mm, "end": v(64.57, -2.76) * mm});
            skLineSegment(sketch, "E372", {"start": v(64.57, -2.76) * mm, "end": v(63.45, -3.57) * mm});
            skLineSegment(sketch, "E373", {"start": v(63.45, -3.57) * mm, "end": v(62.02, -3.96) * mm});
            skLineSegment(sketch, "E374", {"start": v(46.16, -4.38) * mm, "end": v(46.53, -0.02) * mm});
            skLineSegment(sketch, "E375", {"start": v(46.53, -0.02) * mm, "end": v(46.16, 4.33) * mm});
            skLineSegment(sketch, "E376", {"start": v(-0.1, 44.25) * mm, "end": v(-4.63, 44.03) * mm});
            skLineSegment(sketch, "E377", {"start": v(-4.63, 44.03) * mm, "end": v(-9.04, 43.35) * mm});
            skLineSegment(sketch, "E378", {"start": v(-9.04, 43.35) * mm, "end": v(-13.29, 42.26) * mm});
            skLineSegment(sketch, "E379", {"start": v(-13.29, 42.26) * mm, "end": v(-17.36, 40.77) * mm});
            skLineSegment(sketch, "E380", {"start": v(-17.36, 40.77) * mm, "end": v(-21.24, 38.91) * mm});
            skLineSegment(sketch, "E381", {"start": v(-21.24, 38.91) * mm, "end": v(-24.9, 36.7) * mm});
            skLineSegment(sketch, "E382", {"start": v(-24.9, 36.7) * mm, "end": v(-28.31, 34.15) * mm});
            skLineSegment(sketch, "E383", {"start": v(-28.31, 34.15) * mm, "end": v(-31.46, 31.29) * mm});
            skLineSegment(sketch, "E384", {"start": v(-31.46, 31.29) * mm, "end": v(-34.33, 28.15) * mm});
            skLineSegment(sketch, "E385", {"start": v(-34.33, 28.15) * mm, "end": v(-36.88, 24.74) * mm});
            skLineSegment(sketch, "E386", {"start": v(-36.88, 24.74) * mm, "end": v(-39.1, 21.09) * mm});
            skLineSegment(sketch, "E387", {"start": v(-39.1, 21.09) * mm, "end": v(-40.97, 17.22) * mm});
            skLineSegment(sketch, "E388", {"start": v(-40.97, 17.22) * mm, "end": v(-42.46, 13.15) * mm});
            skLineSegment(sketch, "E389", {"start": v(-42.46, 13.15) * mm, "end": v(-43.55, 8.9) * mm});
            skLineSegment(sketch, "E390", {"start": v(-43.55, 8.9) * mm, "end": v(-44.22, 4.51) * mm});
            skLineSegment(sketch, "E391", {"start": v(-44.22, 4.51) * mm, "end": v(-44.45, -0.01) * mm});
            skLineSegment(sketch, "E392", {"start": v(-44.45, -0.01) * mm, "end": v(-44.22, -4.54) * mm});
            skLineSegment(sketch, "E393", {"start": v(-44.22, -4.54) * mm, "end": v(-43.55, -8.93) * mm});
            skLineSegment(sketch, "E394", {"start": v(-43.55, -8.93) * mm, "end": v(-42.46, -13.17) * mm});
            skLineSegment(sketch, "E395", {"start": v(-42.46, -13.17) * mm, "end": v(-40.97, -17.24) * mm});
            skLineSegment(sketch, "E396", {"start": v(-40.97, -17.24) * mm, "end": v(-39.1, -21.11) * mm});
            skLineSegment(sketch, "E397", {"start": v(-39.1, -21.11) * mm, "end": v(-36.88, -24.76) * mm});
            skLineSegment(sketch, "E398", {"start": v(-36.88, -24.76) * mm, "end": v(-34.33, -28.17) * mm});
            skLineSegment(sketch, "E399", {"start": v(-34.33, -28.17) * mm, "end": v(-31.46, -31.31) * mm});
            skLineSegment(sketch, "E400", {"start": v(-31.46, -31.31) * mm, "end": v(-28.31, -34.17) * mm});
            skLineSegment(sketch, "E401", {"start": v(-28.31, -34.17) * mm, "end": v(-24.9, -36.72) * mm});
            skLineSegment(sketch, "E402", {"start": v(-24.9, -36.72) * mm, "end": v(-21.24, -38.93) * mm});
            skLineSegment(sketch, "E403", {"start": v(-21.24, -38.93) * mm, "end": v(-17.36, -40.8) * mm});
            skLineSegment(sketch, "E404", {"start": v(-17.36, -40.8) * mm, "end": v(-13.29, -42.29) * mm});
            skLineSegment(sketch, "E405", {"start": v(-13.29, -42.29) * mm, "end": v(-9.04, -43.38) * mm});
            skLineSegment(sketch, "E406", {"start": v(-9.04, -43.38) * mm, "end": v(-4.63, -44.05) * mm});
            skLineSegment(sketch, "E407", {"start": v(-4.63, -44.05) * mm, "end": v(-0.1, -44.28) * mm});
            skLineSegment(sketch, "E408", {"start": v(-0.1, -44.28) * mm, "end": v(4.43, -44.05) * mm});
            skLineSegment(sketch, "E409", {"start": v(4.43, -44.05) * mm, "end": v(8.84, -43.38) * mm});
            skLineSegment(sketch, "E410", {"start": v(8.84, -43.38) * mm, "end": v(13.09, -42.29) * mm});
            skLineSegment(sketch, "E411", {"start": v(13.09, -42.29) * mm, "end": v(17.16, -40.8) * mm});
            skLineSegment(sketch, "E412", {"start": v(17.16, -40.8) * mm, "end": v(21.04, -38.93) * mm});
            skLineSegment(sketch, "E413", {"start": v(21.04, -38.93) * mm, "end": v(24.7, -36.72) * mm});
            skLineSegment(sketch, "E414", {"start": v(24.7, -36.72) * mm, "end": v(28.11, -34.17) * mm});
            skLineSegment(sketch, "E415", {"start": v(28.11, -34.17) * mm, "end": v(31.26, -31.31) * mm});
            skLineSegment(sketch, "E416", {"start": v(31.26, -31.31) * mm, "end": v(34.13, -28.17) * mm});
            skLineSegment(sketch, "E417", {"start": v(34.13, -28.17) * mm, "end": v(36.68, -24.76) * mm});
            skLineSegment(sketch, "E418", {"start": v(36.68, -24.76) * mm, "end": v(38.9, -21.11) * mm});
            skLineSegment(sketch, "E419", {"start": v(38.9, -21.11) * mm, "end": v(40.77, -17.24) * mm});
            skLineSegment(sketch, "E420", {"start": v(40.77, -17.24) * mm, "end": v(42.26, -13.17) * mm});
            skLineSegment(sketch, "E421", {"start": v(42.26, -13.17) * mm, "end": v(43.35, -8.93) * mm});
            skLineSegment(sketch, "E422", {"start": v(43.35, -8.93) * mm, "end": v(44.02, -4.54) * mm});
            skLineSegment(sketch, "E423", {"start": v(44.02, -4.54) * mm, "end": v(44.25, -0.01) * mm});
            skLineSegment(sketch, "E424", {"start": v(44.25, -0.01) * mm, "end": v(44.02, 4.51) * mm});
            skLineSegment(sketch, "E425", {"start": v(44.02, 4.51) * mm, "end": v(43.35, 8.9) * mm});
            skLineSegment(sketch, "E426", {"start": v(43.35, 8.9) * mm, "end": v(42.26, 13.15) * mm});
            skLineSegment(sketch, "E427", {"start": v(42.26, 13.15) * mm, "end": v(40.77, 17.22) * mm});
            skLineSegment(sketch, "E428", {"start": v(40.77, 17.22) * mm, "end": v(38.9, 21.09) * mm});
            skLineSegment(sketch, "E429", {"start": v(38.9, 21.09) * mm, "end": v(36.68, 24.74) * mm});
            skLineSegment(sketch, "E430", {"start": v(36.68, 24.74) * mm, "end": v(34.13, 28.15) * mm});
            skLineSegment(sketch, "E431", {"start": v(34.13, 28.15) * mm, "end": v(31.26, 31.29) * mm});
            skLineSegment(sketch, "E432", {"start": v(31.26, 31.29) * mm, "end": v(28.11, 34.15) * mm});
            skLineSegment(sketch, "E433", {"start": v(28.11, 34.15) * mm, "end": v(24.7, 36.7) * mm});
            skLineSegment(sketch, "E434", {"start": v(24.7, 36.7) * mm, "end": v(21.04, 38.91) * mm});
            skLineSegment(sketch, "E435", {"start": v(21.04, 38.91) * mm, "end": v(17.16, 40.77) * mm});
            skLineSegment(sketch, "E436", {"start": v(17.16, 40.77) * mm, "end": v(13.09, 42.26) * mm});
            skLineSegment(sketch, "E437", {"start": v(13.09, 42.26) * mm, "end": v(8.84, 43.35) * mm});
            skLineSegment(sketch, "E438", {"start": v(8.84, 43.35) * mm, "end": v(4.43, 44.03) * mm});
            skLineSegment(sketch, "E439", {"start": v(4.43, 44.03) * mm, "end": v(-0.1, 44.25) * mm});
            skLineSegment(sketch, "E440", {"start": v(-0.1, 31.24) * mm, "end": v(6.21, 30.6) * mm});
            skLineSegment(sketch, "E441", {"start": v(6.21, 30.6) * mm, "end": v(12.09, 28.78) * mm});
            skLineSegment(sketch, "E442", {"start": v(12.09, 28.78) * mm, "end": v(17.4, 25.9) * mm});
            skLineSegment(sketch, "E443", {"start": v(17.4, 25.9) * mm, "end": v(22.04, 22.08) * mm});
            skLineSegment(sketch, "E444", {"start": v(22.04, 22.08) * mm, "end": v(25.86, 17.46) * mm});
            skLineSegment(sketch, "E445", {"start": v(25.86, 17.46) * mm, "end": v(28.75, 12.15) * mm});
            skLineSegment(sketch, "E446", {"start": v(28.75, 12.15) * mm, "end": v(30.58, 6.29) * mm});
            skLineSegment(sketch, "E447", {"start": v(30.58, 6.29) * mm, "end": v(31.21, -0.01) * mm});
            skLineSegment(sketch, "E448", {"start": v(31.21, -0.01) * mm, "end": v(30.58, -6.3) * mm});
            skLineSegment(sketch, "E449", {"start": v(30.58, -6.3) * mm, "end": v(28.75, -12.17) * mm});
            skLineSegment(sketch, "E450", {"start": v(28.75, -12.17) * mm, "end": v(25.86, -17.48) * mm});
            skLineSegment(sketch, "E451", {"start": v(25.86, -17.48) * mm, "end": v(22.04, -22.1) * mm});
            skLineSegment(sketch, "E452", {"start": v(22.04, -22.1) * mm, "end": v(17.4, -25.92) * mm});
            skLineSegment(sketch, "E453", {"start": v(17.4, -25.92) * mm, "end": v(12.09, -28.8) * mm});
            skLineSegment(sketch, "E454", {"start": v(12.09, -28.8) * mm, "end": v(6.21, -30.63) * mm});
            skLineSegment(sketch, "E455", {"start": v(6.21, -30.63) * mm, "end": v(-0.1, -31.26) * mm});
            skLineSegment(sketch, "E456", {"start": v(-0.1, -31.26) * mm, "end": v(-6.4, -30.63) * mm});
            skLineSegment(sketch, "E457", {"start": v(-6.4, -30.63) * mm, "end": v(-12.29, -28.8) * mm});
            skLineSegment(sketch, "E458", {"start": v(-12.29, -28.8) * mm, "end": v(-17.6, -25.92) * mm});
            skLineSegment(sketch, "E459", {"start": v(-17.6, -25.92) * mm, "end": v(-22.24, -22.1) * mm});
            skLineSegment(sketch, "E460", {"start": v(-22.24, -22.1) * mm, "end": v(-26.06, -17.48) * mm});
            skLineSegment(sketch, "E461", {"start": v(-26.06, -17.48) * mm, "end": v(-28.95, -12.17) * mm});
            skLineSegment(sketch, "E462", {"start": v(-28.95, -12.17) * mm, "end": v(-30.78, -6.3) * mm});
            skLineSegment(sketch, "E463", {"start": v(-30.78, -6.3) * mm, "end": v(-31.41, -0.01) * mm});
            skLineSegment(sketch, "E464", {"start": v(-31.41, -0.01) * mm, "end": v(-30.78, 6.29) * mm});
            skLineSegment(sketch, "E465", {"start": v(-30.78, 6.29) * mm, "end": v(-28.95, 12.15) * mm});
            skLineSegment(sketch, "E466", {"start": v(-28.95, 12.15) * mm, "end": v(-26.06, 17.46) * mm});
            skLineSegment(sketch, "E467", {"start": v(-26.06, 17.46) * mm, "end": v(-22.24, 22.08) * mm});
            skLineSegment(sketch, "E468", {"start": v(-22.24, 22.08) * mm, "end": v(-17.6, 25.9) * mm});
            skLineSegment(sketch, "E469", {"start": v(-17.6, 25.9) * mm, "end": v(-12.29, 28.78) * mm});
            skLineSegment(sketch, "E470", {"start": v(-12.29, 28.78) * mm, "end": v(-6.4, 30.6) * mm});
            skLineSegment(sketch, "E471", {"start": v(-6.4, 30.6) * mm, "end": v(-0.1, 31.24) * mm});
            skLineSegment(sketch, "E472", {"start": v(-2.76, -2.56) * mm, "end": v(-5.7, -5.5) * mm});
            skLineSegment(sketch, "E473", {"start": v(6.03, 6.2) * mm, "end": v(2.4, 2.58) * mm});
            skLineSegment(sketch, "E474", {"start": v(2.65, -2.35) * mm, "end": v(5.6, -5.28) * mm});
            skLineSegment(sketch, "E475", {"start": v(-6.14, 6.43) * mm, "end": v(-2.5, 2.8) * mm});
            skLineSegment(sketch, "E476", {"start": v(-3.75, -0.01) * mm, "end": v(-8.24, -0.01) * mm});
            skLineSegment(sketch, "E477", {"start": v(8.35, -0.01) * mm, "end": v(3.56, -0.01) * mm});
            skLineSegment(sketch, "E478", {"start": v(-0.1, -3.68) * mm, "end": v(-0.1, -7.83) * mm});
            skLineSegment(sketch, "E479", {"start": v(-0.1, 8.73) * mm, "end": v(-0.1, 3.6) * mm});
            skLineSegment(sketch, "E480", {"start": v(32.3, -0.01) * mm, "end": v(31.64, -6.53) * mm});
            skLineSegment(sketch, "E481", {"start": v(31.64, -6.53) * mm, "end": v(29.75, -12.6) * mm});
            skLineSegment(sketch, "E482", {"start": v(29.75, -12.6) * mm, "end": v(26.76, -18.09) * mm});
            skLineSegment(sketch, "E483", {"start": v(26.76, -18.09) * mm, "end": v(22.8, -22.87) * mm});
            skLineSegment(sketch, "E484", {"start": v(22.8, -22.87) * mm, "end": v(18.01, -26.82) * mm});
            skLineSegment(sketch, "E485", {"start": v(18.01, -26.82) * mm, "end": v(12.5, -29.8) * mm});
            skLineSegment(sketch, "E486", {"start": v(12.5, -29.8) * mm, "end": v(6.43, -31.69) * mm});
            skLineSegment(sketch, "E487", {"start": v(6.43, -31.69) * mm, "end": v(-0.1, -32.34) * mm});
            skLineSegment(sketch, "E488", {"start": v(-0.1, -32.34) * mm, "end": v(-6.63, -31.69) * mm});
            skLineSegment(sketch, "E489", {"start": v(-6.63, -31.69) * mm, "end": v(-12.7, -29.8) * mm});
            skLineSegment(sketch, "E490", {"start": v(-12.7, -29.8) * mm, "end": v(-18.21, -26.82) * mm});
            skLineSegment(sketch, "E491", {"start": v(-18.21, -26.82) * mm, "end": v(-23, -22.87) * mm});
            skLineSegment(sketch, "E492", {"start": v(-23, -22.87) * mm, "end": v(-26.96, -18.09) * mm});
            skLineSegment(sketch, "E493", {"start": v(-26.96, -18.09) * mm, "end": v(-29.95, -12.6) * mm});
            skLineSegment(sketch, "E494", {"start": v(-29.95, -12.6) * mm, "end": v(-31.84, -6.53) * mm});
            skLineSegment(sketch, "E495", {"start": v(-31.84, -6.53) * mm, "end": v(-32.5, -0.01) * mm});
            skLineSegment(sketch, "E496", {"start": v(-32.5, -0.01) * mm, "end": v(-31.84, 6.5) * mm});
            skLineSegment(sketch, "E497", {"start": v(-31.84, 6.5) * mm, "end": v(-29.95, 12.57) * mm});
            skLineSegment(sketch, "E498", {"start": v(-29.95, 12.57) * mm, "end": v(-26.96, 18.06) * mm});
            skLineSegment(sketch, "E499", {"start": v(-26.96, 18.06) * mm, "end": v(-23, 22.85) * mm});
            skLineSegment(sketch, "E500", {"start": v(-23, 22.85) * mm, "end": v(-18.21, 26.8) * mm});
            skLineSegment(sketch, "E501", {"start": v(-18.21, 26.8) * mm, "end": v(-12.7, 29.78) * mm});
            skLineSegment(sketch, "E502", {"start": v(-12.7, 29.78) * mm, "end": v(-6.63, 31.66) * mm});
            skLineSegment(sketch, "E503", {"start": v(-6.63, 31.66) * mm, "end": v(-0.1, 32.32) * mm});
            skLineSegment(sketch, "E504", {"start": v(-0.1, 32.32) * mm, "end": v(6.43, 31.66) * mm});
            skLineSegment(sketch, "E505", {"start": v(6.43, 31.66) * mm, "end": v(12.5, 29.78) * mm});
            skLineSegment(sketch, "E506", {"start": v(12.5, 29.78) * mm, "end": v(18.01, 26.8) * mm});
            skLineSegment(sketch, "E507", {"start": v(18.01, 26.8) * mm, "end": v(22.8, 22.85) * mm});
            skLineSegment(sketch, "E508", {"start": v(22.8, 22.85) * mm, "end": v(26.76, 18.06) * mm});
            skLineSegment(sketch, "E509", {"start": v(26.76, 18.06) * mm, "end": v(29.75, 12.57) * mm});
            skLineSegment(sketch, "E510", {"start": v(29.75, 12.57) * mm, "end": v(31.64, 6.5) * mm});
            skLineSegment(sketch, "E511", {"start": v(31.64, 6.5) * mm, "end": v(32.3, -0.01) * mm});
            skLineSegment(sketch, "E512", {"start": v(-0.1, 10.82) * mm, "end": v(-2.29, 10.6) * mm});
            skLineSegment(sketch, "E513", {"start": v(-2.29, 10.6) * mm, "end": v(-4.33, 9.97) * mm});
            skLineSegment(sketch, "E514", {"start": v(-4.33, 9.97) * mm, "end": v(-6.17, 8.97) * mm});
            skLineSegment(sketch, "E515", {"start": v(-6.17, 8.97) * mm, "end": v(-7.78, 7.65) * mm});
            skLineSegment(sketch, "E516", {"start": v(-7.78, 7.65) * mm, "end": v(-9.1, 6.05) * mm});
            skLineSegment(sketch, "E517", {"start": v(-9.1, 6.05) * mm, "end": v(-10.1, 4.2) * mm});
            skLineSegment(sketch, "E518", {"start": v(-10.1, 4.2) * mm, "end": v(-10.73, 2.17) * mm});
            skLineSegment(sketch, "E519", {"start": v(-10.73, 2.17) * mm, "end": v(-10.96, -0.01) * mm});
            skLineSegment(sketch, "E520", {"start": v(-10.96, -0.01) * mm, "end": v(-10.73, -2.2) * mm});
            skLineSegment(sketch, "E521", {"start": v(-10.73, -2.2) * mm, "end": v(-10.1, -4.23) * mm});
            skLineSegment(sketch, "E522", {"start": v(-10.1, -4.23) * mm, "end": v(-9.1, -6.07) * mm});
            skLineSegment(sketch, "E523", {"start": v(-9.1, -6.07) * mm, "end": v(-7.78, -7.67) * mm});
            skLineSegment(sketch, "E524", {"start": v(-7.78, -7.67) * mm, "end": v(-6.17, -9) * mm});
            skLineSegment(sketch, "E525", {"start": v(-6.17, -9) * mm, "end": v(-4.33, -10) * mm});
            skLineSegment(sketch, "E526", {"start": v(-4.33, -10) * mm, "end": v(-2.29, -10.63) * mm});
            skLineSegment(sketch, "E527", {"start": v(-2.29, -10.63) * mm, "end": v(-0.1, -10.85) * mm});
            skLineSegment(sketch, "E528", {"start": v(-0.1, -10.85) * mm, "end": v(2.09, -10.63) * mm});
            skLineSegment(sketch, "E529", {"start": v(2.09, -10.63) * mm, "end": v(4.13, -10) * mm});
            skLineSegment(sketch, "E530", {"start": v(4.13, -10) * mm, "end": v(5.97, -9) * mm});
            skLineSegment(sketch, "E531", {"start": v(5.97, -9) * mm, "end": v(7.58, -7.67) * mm});
            skLineSegment(sketch, "E532", {"start": v(7.58, -7.67) * mm, "end": v(8.9, -6.07) * mm});
            skLineSegment(sketch, "E533", {"start": v(8.9, -6.07) * mm, "end": v(9.9, -4.23) * mm});
            skLineSegment(sketch, "E534", {"start": v(9.9, -4.23) * mm, "end": v(10.54, -2.2) * mm});
            skLineSegment(sketch, "E535", {"start": v(10.54, -2.2) * mm, "end": v(10.76, -0.01) * mm});
            skLineSegment(sketch, "E536", {"start": v(10.76, -0.01) * mm, "end": v(10.54, 2.17) * mm});
            skLineSegment(sketch, "E537", {"start": v(10.54, 2.17) * mm, "end": v(9.9, 4.2) * mm});
            skLineSegment(sketch, "E538", {"start": v(9.9, 4.2) * mm, "end": v(8.9, 6.05) * mm});
            skLineSegment(sketch, "E539", {"start": v(8.9, 6.05) * mm, "end": v(7.58, 7.65) * mm});
            skLineSegment(sketch, "E540", {"start": v(7.58, 7.65) * mm, "end": v(5.97, 8.97) * mm});
            skLineSegment(sketch, "E541", {"start": v(5.97, 8.97) * mm, "end": v(4.13, 9.97) * mm});
            skLineSegment(sketch, "E542", {"start": v(4.13, 9.97) * mm, "end": v(2.09, 10.6) * mm});
            skLineSegment(sketch, "E543", {"start": v(2.09, 10.6) * mm, "end": v(-0.1, 10.82) * mm});
            skLineSegment(sketch, "E544", {"start": v(-0.1, 7.29) * mm, "end": v(2.75, 6.72) * mm});
            skLineSegment(sketch, "E545", {"start": v(2.75, 6.72) * mm, "end": v(5.07, 5.15) * mm});
            skLineSegment(sketch, "E546", {"start": v(5.07, 5.15) * mm, "end": v(6.64, 2.83) * mm});
            skLineSegment(sketch, "E547", {"start": v(6.64, 2.83) * mm, "end": v(7.22, -0.01) * mm});
            skLineSegment(sketch, "E548", {"start": v(7.22, -0.01) * mm, "end": v(6.64, -2.85) * mm});
            skLineSegment(sketch, "E549", {"start": v(6.64, -2.85) * mm, "end": v(5.07, -5.17) * mm});
            skLineSegment(sketch, "E550", {"start": v(5.07, -5.17) * mm, "end": v(2.75, -6.74) * mm});
            skLineSegment(sketch, "E551", {"start": v(2.75, -6.74) * mm, "end": v(-0.1, -7.31) * mm});
            skLineSegment(sketch, "E552", {"start": v(-0.1, -7.31) * mm, "end": v(-2.95, -6.74) * mm});
            skLineSegment(sketch, "E553", {"start": v(-2.95, -6.74) * mm, "end": v(-5.27, -5.17) * mm});
            skLineSegment(sketch, "E554", {"start": v(-5.27, -5.17) * mm, "end": v(-6.84, -2.85) * mm});
            skLineSegment(sketch, "E555", {"start": v(-6.84, -2.85) * mm, "end": v(-7.41, -0.01) * mm});
            skLineSegment(sketch, "E556", {"start": v(-7.41, -0.01) * mm, "end": v(-6.84, 2.83) * mm});
            skLineSegment(sketch, "E557", {"start": v(-6.84, 2.83) * mm, "end": v(-5.27, 5.15) * mm});
            skLineSegment(sketch, "E558", {"start": v(-5.27, 5.15) * mm, "end": v(-2.95, 6.72) * mm});
            skLineSegment(sketch, "E559", {"start": v(-2.95, 6.72) * mm, "end": v(-0.1, 7.29) * mm});
            skLineSegment(sketch, "E560", {"start": v(-28.38, 34.25) * mm, "end": v(-28.31, 34.15) * mm});
            skLineSegment(sketch, "E561", {"start": v(-34.45, 28.18) * mm, "end": v(-34.37, 28.1) * mm});
            skLineSegment(sketch, "E562", {"start": v(-4.43, 44.17) * mm, "end": v(-4.43, 44.04) * mm});
            skLineSegment(sketch, "E563", {"start": v(4.17, 44.17) * mm, "end": v(4.17, 44.04) * mm});
            skLineSegment(sketch, "E564", {"start": v(34.22, 28.22) * mm, "end": v(34.13, 28.14) * mm});
            skLineSegment(sketch, "E565", {"start": v(44.13, 4.25) * mm, "end": v(44.04, 4.25) * mm});
            skLineSegment(sketch, "E566", {"start": v(44.13, -4.33) * mm, "end": v(44.03, -4.33) * mm});
            skLineSegment(sketch, "E567", {"start": v(28.18, -34.25) * mm, "end": v(28.1, -34.18) * mm});
            skLineSegment(sketch, "E568", {"start": v(4.23, -44.17) * mm, "end": v(4.23, -44.06) * mm});
            skLineSegment(sketch, "E569", {"start": v(-4.37, -44.17) * mm, "end": v(-4.37, -44.06) * mm});
            skLineSegment(sketch, "E570", {"start": v(28.14, 34.29) * mm, "end": v(28.05, 34.2) * mm});
            skLineSegment(sketch, "E571", {"start": v(34.26, -28.18) * mm, "end": v(34.18, -28.1) * mm});
            skLineSegment(sketch, "E572", {"start": v(-28.34, -34.29) * mm, "end": v(-28.26, -34.2) * mm});
            skLineSegment(sketch, "E573", {"start": v(-34.41, -28.22) * mm, "end": v(-34.34, -28.15) * mm});
            skSolve(sketch);
        }
        {
            var Q0;
            Q0=qSketchRegion(id+"F0",true);
            var Q1;
            {var subQ0=sQuery(id+"F0.wireOp",EDGE,"E384");var subQ1=sQuery(id+"F0.wireOp",EDGE,"E205");var subQ2=makeQuery(id+"F0.imprint","INTERSECT",VERTEX,{"derivedFrom":[subQ1,subQ0]});Q1=makeQuery(id+"F0.imprint","IMPRINT",FACE,{"disambiguationData":[TD([[makeQuery(id+"F0.imprint","IMPRINT",EDGE,{"disambiguationData":[TD([[subQ2,-1.0]])],"derivedFrom":subQ1}),1.0]])]});}
            var Q2;
            {var subQ0=sQuery(id+"F0.wireOp",EDGE,"E376");var subQ1=sQuery(id+"F0.wireOp",EDGE,"E115");var subQ2=makeQuery(id+"F0.imprint","INTERSECT",VERTEX,{"derivedFrom":[subQ1,subQ0]});Q2=makeQuery(id+"F0.imprint","IMPRINT",FACE,{"disambiguationData":[TD([[makeQuery(id+"F0.imprint","IMPRINT",EDGE,{"disambiguationData":[TD([[subQ2,-1.0]])],"derivedFrom":subQ1}),1.0]])]});}
            var Q3;
            {var subQ0=sQuery(id+"F0.wireOp",EDGE,"E408");var subQ1=sQuery(id+"F0.wireOp",EDGE,"E70");var subQ2=makeQuery(id+"F0.imprint","INTERSECT",VERTEX,{"derivedFrom":[subQ1,subQ0]});Q3=makeQuery(id+"F0.imprint","IMPRINT",FACE,{"disambiguationData":[TD([[makeQuery(id+"F0.imprint","IMPRINT",EDGE,{"disambiguationData":[TD([[subQ2,-1.0]])],"derivedFrom":subQ1}),1.0]])]});}
            var Q4;
            {var subQ0=sQuery(id+"F0.wireOp",EDGE,"E416");var subQ1=sQuery(id+"F0.wireOp",EDGE,"E160");var subQ2=makeQuery(id+"F0.imprint","INTERSECT",VERTEX,{"derivedFrom":[subQ1,subQ0]});Q4=makeQuery(id+"F0.imprint","IMPRINT",FACE,{"disambiguationData":[TD([[makeQuery(id+"F0.imprint","IMPRINT",EDGE,{"disambiguationData":[TD([[subQ2,-1.0]])],"derivedFrom":subQ1}),1.0]])]});}
            var Q5;
            {var subQ0=sQuery(id+"F0.wireOp",EDGE,"E423");var subQ1=sQuery(id+"F0.wireOp",EDGE,"E356");var subQ2=makeQuery(id+"F0.imprint","INTERSECT",VERTEX,{"derivedFrom":[subQ1,subQ0]});Q5=makeQuery(id+"F0.imprint","IMPRINT",FACE,{"disambiguationData":[TD([[makeQuery(id+"F0.imprint","IMPRINT",EDGE,{"disambiguationData":[TD([[subQ2,-1.0]])],"derivedFrom":subQ1}),-1.0]])]});}
            var Q6;
            {var subQ0=sQuery(id+"F0.wireOp",EDGE,"E432");var subQ1=sQuery(id+"F0.wireOp",EDGE,"E295");var subQ2=makeQuery(id+"F0.imprint","INTERSECT",VERTEX,{"derivedFrom":[subQ1,subQ0]});Q6=makeQuery(id+"F0.imprint","IMPRINT",FACE,{"disambiguationData":[TD([[makeQuery(id+"F0.imprint","IMPRINT",EDGE,{"disambiguationData":[TD([[subQ2,-1.0]])],"derivedFrom":subQ1}),1.0]])]});}
            var Q7;
            {var subQ0=sQuery(id+"F0.wireOp",EDGE,"E400");var subQ1=sQuery(id+"F0.wireOp",EDGE,"E250");var subQ2=makeQuery(id+"F0.imprint","INTERSECT",VERTEX,{"derivedFrom":[subQ1,subQ0]});Q7=makeQuery(id+"F0.imprint","IMPRINT",FACE,{"disambiguationData":[TD([[makeQuery(id+"F0.imprint","IMPRINT",EDGE,{"disambiguationData":[TD([[subQ2,-1.0]])],"derivedFrom":subQ1}),1.0]])]});}
            extrude(context, id + "F1", {"entities" : qUnion([Q0, Q1, Q2, Q3, Q4, Q5, Q6, Q7]), "depth" : 3.17 * mm});
        }
        {
            var Q0;
            Q0=makeQuery(id+"F1.opExtrude","CAP_FACE",FACE,{"disambiguationData":[OSD([sQuery(id+"F0.wireOp",EDGE,"E16"),sQuery(id+"F0.wireOp",EDGE,"E17"),sQuery(id+"F0.wireOp",EDGE,"E18"),sQuery(id+"F0.wireOp",EDGE,"E19"),sQuery(id+"F0.wireOp",EDGE,"E20"),sQuery(id+"F0.wireOp",EDGE,"E21"),sQuery(id+"F0.wireOp",EDGE,"E22"),sQuery(id+"F0.wireOp",EDGE,"E23"),sQuery(id+"F0.wireOp",EDGE,"E24"),sQuery(id+"F0.wireOp",EDGE,"E26"),sQuery(id+"F0.wireOp",EDGE,"E27"),sQuery(id+"F0.wireOp",EDGE,"E28"),sQuery(id+"F0.wireOp",EDGE,"E29"),sQuery(id+"F0.wireOp",EDGE,"E30"),sQuery(id+"F0.wireOp",EDGE,"E31"),sQuery(id+"F0.wireOp",EDGE,"E32"),sQuery(id+"F0.wireOp",EDGE,"E33"),sQuery(id+"F0.wireOp",EDGE,"E34"),sQuery(id+"F0.wireOp",EDGE,"E35"),sQuery(id+"F0.wireOp",EDGE,"E36"),sQuery(id+"F0.wireOp",EDGE,"E37"),sQuery(id+"F0.wireOp",EDGE,"E38"),sQuery(id+"F0.wireOp",EDGE,"E39"),sQuery(id+"F0.wireOp",EDGE,"E40"),sQuery(id+"F0.wireOp",EDGE,"E41"),sQuery(id+"F0.wireOp",EDGE,"E42"),sQuery(id+"F0.wireOp",EDGE,"E61"),sQuery(id+"F0.wireOp",EDGE,"E62"),sQuery(id+"F0.wireOp",EDGE,"E63"),sQuery(id+"F0.wireOp",EDGE,"E64"),sQuery(id+"F0.wireOp",EDGE,"E65"),sQuery(id+"F0.wireOp",EDGE,"E66"),sQuery(id+"F0.wireOp",EDGE,"E67"),sQuery(id+"F0.wireOp",EDGE,"E68"),sQuery(id+"F0.wireOp",EDGE,"E69"),sQuery(id+"F0.wireOp",EDGE,"E70"),sQuery(id+"F0.wireOp",EDGE,"E71"),sQuery(id+"F0.wireOp",EDGE,"E72"),sQuery(id+"F0.wireOp",EDGE,"E73"),sQuery(id+"F0.wireOp",EDGE,"E74"),sQuery(id+"F0.wireOp",EDGE,"E75"),sQuery(id+"F0.wireOp",EDGE,"E76"),sQuery(id+"F0.wireOp",EDGE,"E77"),sQuery(id+"F0.wireOp",EDGE,"E78"),sQuery(id+"F0.wireOp",EDGE,"E79"),sQuery(id+"F0.wireOp",EDGE,"E80"),sQuery(id+"F0.wireOp",EDGE,"E81"),sQuery(id+"F0.wireOp",EDGE,"E82"),sQuery(id+"F0.wireOp",EDGE,"E83"),sQuery(id+"F0.wireOp",EDGE,"E84"),sQuery(id+"F0.wireOp",EDGE,"E85"),sQuery(id+"F0.wireOp",EDGE,"E86"),sQuery(id+"F0.wireOp",EDGE,"E87"),sQuery(id+"F0.wireOp",EDGE,"E106"),sQuery(id+"F0.wireOp",EDGE,"E107"),sQuery(id+"F0.wireOp",EDGE,"E108"),sQuery(id+"F0.wireOp",EDGE,"E109"),sQuery(id+"F0.wireOp",EDGE,"E110"),sQuery(id+"F0.wireOp",EDGE,"E111"),sQuery(id+"F0.wireOp",EDGE,"E112"),sQuery(id+"F0.wireOp",EDGE,"E113"),sQuery(id+"F0.wireOp",EDGE,"E114"),sQuery(id+"F0.wireOp",EDGE,"E115"),sQuery(id+"F0.wireOp",EDGE,"E116"),sQuery(id+"F0.wireOp",EDGE,"E117"),sQuery(id+"F0.wireOp",EDGE,"E118"),sQuery(id+"F0.wireOp",EDGE,"E119"),sQuery(id+"F0.wireOp",EDGE,"E120"),sQuery(id+"F0.wireOp",EDGE,"E121"),sQuery(id+"F0.wireOp",EDGE,"E122"),sQuery(id+"F0.wireOp",EDGE,"E123"),sQuery(id+"F0.wireOp",EDGE,"E124"),sQuery(id+"F0.wireOp",EDGE,"E125"),sQuery(id+"F0.wireOp",EDGE,"E126"),sQuery(id+"F0.wireOp",EDGE,"E127"),sQuery(id+"F0.wireOp",EDGE,"E128"),sQuery(id+"F0.wireOp",EDGE,"E129"),sQuery(id+"F0.wireOp",EDGE,"E130"),sQuery(id+"F0.wireOp",EDGE,"E131"),sQuery(id+"F0.wireOp",EDGE,"E132"),sQuery(id+"F0.wireOp",EDGE,"E169"),sQuery(id+"F0.wireOp",EDGE,"E170"),sQuery(id+"F0.wireOp",EDGE,"E151"),sQuery(id+"F0.wireOp",EDGE,"E152"),sQuery(id+"F0.wireOp",EDGE,"E153"),sQuery(id+"F0.wireOp",EDGE,"E154"),sQuery(id+"F0.wireOp",EDGE,"E155"),sQuery(id+"F0.wireOp",EDGE,"E156"),sQuery(id+"F0.wireOp",EDGE,"E157"),sQuery(id+"F0.wireOp",EDGE,"E158"),sQuery(id+"F0.wireOp",EDGE,"E159"),sQuery(id+"F0.wireOp",EDGE,"E160"),sQuery(id+"F0.wireOp",EDGE,"E161"),sQuery(id+"F0.wireOp",EDGE,"E162"),sQuery(id+"F0.wireOp",EDGE,"E163"),sQuery(id+"F0.wireOp",EDGE,"E164"),sQuery(id+"F0.wireOp",EDGE,"E165"),sQuery(id+"F0.wireOp",EDGE,"E166"),sQuery(id+"F0.wireOp",EDGE,"E167"),sQuery(id+"F0.wireOp",EDGE,"E168"),sQuery(id+"F0.wireOp",EDGE,"E171"),sQuery(id+"F0.wireOp",EDGE,"E172"),sQuery(id+"F0.wireOp",EDGE,"E173"),sQuery(id+"F0.wireOp",EDGE,"E174"),sQuery(id+"F0.wireOp",EDGE,"E175"),sQuery(id+"F0.wireOp",EDGE,"E176"),sQuery(id+"F0.wireOp",EDGE,"E177"),sQuery(id+"F0.wireOp",EDGE,"E196"),sQuery(id+"F0.wireOp",EDGE,"E197"),sQuery(id+"F0.wireOp",EDGE,"E198"),sQuery(id+"F0.wireOp",EDGE,"E199"),sQuery(id+"F0.wireOp",EDGE,"E200"),sQuery(id+"F0.wireOp",EDGE,"E201"),sQuery(id+"F0.wireOp",EDGE,"E202"),sQuery(id+"F0.wireOp",EDGE,"E203"),sQuery(id+"F0.wireOp",EDGE,"E204"),sQuery(id+"F0.wireOp",EDGE,"E205"),sQuery(id+"F0.wireOp",EDGE,"E206"),sQuery(id+"F0.wireOp",EDGE,"E207"),sQuery(id+"F0.wireOp",EDGE,"E208"),sQuery(id+"F0.wireOp",EDGE,"E209"),sQuery(id+"F0.wireOp",EDGE,"E210"),sQuery(id+"F0.wireOp",EDGE,"E211"),sQuery(id+"F0.wireOp",EDGE,"E212"),sQuery(id+"F0.wireOp",EDGE,"E213"),sQuery(id+"F0.wireOp",EDGE,"E214"),sQuery(id+"F0.wireOp",EDGE,"E215"),sQuery(id+"F0.wireOp",EDGE,"E216"),sQuery(id+"F0.wireOp",EDGE,"E217"),sQuery(id+"F0.wireOp",EDGE,"E218"),sQuery(id+"F0.wireOp",EDGE,"E219"),sQuery(id+"F0.wireOp",EDGE,"E220"),sQuery(id+"F0.wireOp",EDGE,"E221"),sQuery(id+"F0.wireOp",EDGE,"E222"),sQuery(id+"F0.wireOp",EDGE,"E241"),sQuery(id+"F0.wireOp",EDGE,"E242"),sQuery(id+"F0.wireOp",EDGE,"E243"),sQuery(id+"F0.wireOp",EDGE,"E244"),sQuery(id+"F0.wireOp",EDGE,"E245"),sQuery(id+"F0.wireOp",EDGE,"E246"),sQuery(id+"F0.wireOp",EDGE,"E247"),sQuery(id+"F0.wireOp",EDGE,"E248"),sQuery(id+"F0.wireOp",EDGE,"E249"),sQuery(id+"F0.wireOp",EDGE,"E250"),sQuery(id+"F0.wireOp",EDGE,"E251"),sQuery(id+"F0.wireOp",EDGE,"E252"),sQuery(id+"F0.wireOp",EDGE,"E253"),sQuery(id+"F0.wireOp",EDGE,"E254"),sQuery(id+"F0.wireOp",EDGE,"E255"),sQuery(id+"F0.wireOp",EDGE,"E256"),sQuery(id+"F0.wireOp",EDGE,"E257"),sQuery(id+"F0.wireOp",EDGE,"E258"),sQuery(id+"F0.wireOp",EDGE,"E259"),sQuery(id+"F0.wireOp",EDGE,"E260"),sQuery(id+"F0.wireOp",EDGE,"E261"),sQuery(id+"F0.wireOp",EDGE,"E262"),sQuery(id+"F0.wireOp",EDGE,"E263"),sQuery(id+"F0.wireOp",EDGE,"E264"),sQuery(id+"F0.wireOp",EDGE,"E265"),sQuery(id+"F0.wireOp",EDGE,"E266"),sQuery(id+"F0.wireOp",EDGE,"E267"),sQuery(id+"F0.wireOp",EDGE,"E286"),sQuery(id+"F0.wireOp",EDGE,"E287"),sQuery(id+"F0.wireOp",EDGE,"E288"),sQuery(id+"F0.wireOp",EDGE,"E289"),sQuery(id+"F0.wireOp",EDGE,"E290"),sQuery(id+"F0.wireOp",EDGE,"E291"),sQuery(id+"F0.wireOp",EDGE,"E292"),sQuery(id+"F0.wireOp",EDGE,"E293"),sQuery(id+"F0.wireOp",EDGE,"E294"),sQuery(id+"F0.wireOp",EDGE,"E295"),sQuery(id+"F0.wireOp",EDGE,"E296"),sQuery(id+"F0.wireOp",EDGE,"E297"),sQuery(id+"F0.wireOp",EDGE,"E298"),sQuery(id+"F0.wireOp",EDGE,"E299"),sQuery(id+"F0.wireOp",EDGE,"E300"),sQuery(id+"F0.wireOp",EDGE,"E301"),sQuery(id+"F0.wireOp",EDGE,"E302"),sQuery(id+"F0.wireOp",EDGE,"E303"),sQuery(id+"F0.wireOp",EDGE,"E304"),sQuery(id+"F0.wireOp",EDGE,"E305"),sQuery(id+"F0.wireOp",EDGE,"E306"),sQuery(id+"F0.wireOp",EDGE,"E307"),sQuery(id+"F0.wireOp",EDGE,"E308"),sQuery(id+"F0.wireOp",EDGE,"E309"),sQuery(id+"F0.wireOp",EDGE,"E310"),sQuery(id+"F0.wireOp",EDGE,"E311"),sQuery(id+"F0.wireOp",EDGE,"E312"),sQuery(id+"F0.wireOp",EDGE,"E347"),sQuery(id+"F0.wireOp",EDGE,"E348"),sQuery(id+"F0.wireOp",EDGE,"E349"),sQuery(id+"F0.wireOp",EDGE,"E350"),sQuery(id+"F0.wireOp",EDGE,"E351"),sQuery(id+"F0.wireOp",EDGE,"E352"),sQuery(id+"F0.wireOp",EDGE,"E353"),sQuery(id+"F0.wireOp",EDGE,"E354"),sQuery(id+"F0.wireOp",EDGE,"E355"),sQuery(id+"F0.wireOp",EDGE,"E356"),sQuery(id+"F0.wireOp",EDGE,"E357"),sQuery(id+"F0.wireOp",EDGE,"E358"),sQuery(id+"F0.wireOp",EDGE,"E359"),sQuery(id+"F0.wireOp",EDGE,"E360"),sQuery(id+"F0.wireOp",EDGE,"E361"),sQuery(id+"F0.wireOp",EDGE,"E362"),sQuery(id+"F0.wireOp",EDGE,"E363"),sQuery(id+"F0.wireOp",EDGE,"E364"),sQuery(id+"F0.wireOp",EDGE,"E365"),sQuery(id+"F0.wireOp",EDGE,"E366"),sQuery(id+"F0.wireOp",EDGE,"E367"),sQuery(id+"F0.wireOp",EDGE,"E368"),sQuery(id+"F0.wireOp",EDGE,"E369"),sQuery(id+"F0.wireOp",EDGE,"E370"),sQuery(id+"F0.wireOp",EDGE,"E371"),sQuery(id+"F0.wireOp",EDGE,"E372"),sQuery(id+"F0.wireOp",EDGE,"E373"),sQuery(id+"F0.wireOp",EDGE,"E376"),sQuery(id+"F0.wireOp",EDGE,"E377"),sQuery(id+"F0.wireOp",EDGE,"E378"),sQuery(id+"F0.wireOp",EDGE,"E379"),sQuery(id+"F0.wireOp",EDGE,"E380"),sQuery(id+"F0.wireOp",EDGE,"E381"),sQuery(id+"F0.wireOp",EDGE,"E382"),sQuery(id+"F0.wireOp",EDGE,"E383"),sQuery(id+"F0.wireOp",EDGE,"E384"),sQuery(id+"F0.wireOp",EDGE,"E385"),sQuery(id+"F0.wireOp",EDGE,"E386"),sQuery(id+"F0.wireOp",EDGE,"E387"),sQuery(id+"F0.wireOp",EDGE,"E388"),sQuery(id+"F0.wireOp",EDGE,"E389"),sQuery(id+"F0.wireOp",EDGE,"E390"),sQuery(id+"F0.wireOp",EDGE,"E391"),sQuery(id+"F0.wireOp",EDGE,"E392"),sQuery(id+"F0.wireOp",EDGE,"E393"),sQuery(id+"F0.wireOp",EDGE,"E394"),sQuery(id+"F0.wireOp",EDGE,"E395"),sQuery(id+"F0.wireOp",EDGE,"E396"),sQuery(id+"F0.wireOp",EDGE,"E397"),sQuery(id+"F0.wireOp",EDGE,"E398"),sQuery(id+"F0.wireOp",EDGE,"E399"),sQuery(id+"F0.wireOp",EDGE,"E400"),sQuery(id+"F0.wireOp",EDGE,"E401"),sQuery(id+"F0.wireOp",EDGE,"E402"),sQuery(id+"F0.wireOp",EDGE,"E403"),sQuery(id+"F0.wireOp",EDGE,"E404"),sQuery(id+"F0.wireOp",EDGE,"E405"),sQuery(id+"F0.wireOp",EDGE,"E406"),sQuery(id+"F0.wireOp",EDGE,"E407"),sQuery(id+"F0.wireOp",EDGE,"E408"),sQuery(id+"F0.wireOp",EDGE,"E409"),sQuery(id+"F0.wireOp",EDGE,"E410"),sQuery(id+"F0.wireOp",EDGE,"E411"),sQuery(id+"F0.wireOp",EDGE,"E412"),sQuery(id+"F0.wireOp",EDGE,"E413"),sQuery(id+"F0.wireOp",EDGE,"E414"),sQuery(id+"F0.wireOp",EDGE,"E415"),sQuery(id+"F0.wireOp",EDGE,"E416"),sQuery(id+"F0.wireOp",EDGE,"E417"),sQuery(id+"F0.wireOp",EDGE,"E418"),sQuery(id+"F0.wireOp",EDGE,"E419"),sQuery(id+"F0.wireOp",EDGE,"E420"),sQuery(id+"F0.wireOp",EDGE,"E421"),sQuery(id+"F0.wireOp",EDGE,"E422"),sQuery(id+"F0.wireOp",EDGE,"E423"),sQuery(id+"F0.wireOp",EDGE,"E424"),sQuery(id+"F0.wireOp",EDGE,"E425"),sQuery(id+"F0.wireOp",EDGE,"E426"),sQuery(id+"F0.wireOp",EDGE,"E427"),sQuery(id+"F0.wireOp",EDGE,"E428"),sQuery(id+"F0.wireOp",EDGE,"E429"),sQuery(id+"F0.wireOp",EDGE,"E430"),sQuery(id+"F0.wireOp",EDGE,"E431"),sQuery(id+"F0.wireOp",EDGE,"E432"),sQuery(id+"F0.wireOp",EDGE,"E433"),sQuery(id+"F0.wireOp",EDGE,"E434"),sQuery(id+"F0.wireOp",EDGE,"E435"),sQuery(id+"F0.wireOp",EDGE,"E436"),sQuery(id+"F0.wireOp",EDGE,"E437"),sQuery(id+"F0.wireOp",EDGE,"E438"),sQuery(id+"F0.wireOp",EDGE,"E439"),sQuery(id+"F0.wireOp",EDGE,"E480"),sQuery(id+"F0.wireOp",EDGE,"E481"),sQuery(id+"F0.wireOp",EDGE,"E482"),sQuery(id+"F0.wireOp",EDGE,"E483"),sQuery(id+"F0.wireOp",EDGE,"E484"),sQuery(id+"F0.wireOp",EDGE,"E485"),sQuery(id+"F0.wireOp",EDGE,"E486"),sQuery(id+"F0.wireOp",EDGE,"E487"),sQuery(id+"F0.wireOp",EDGE,"E488"),sQuery(id+"F0.wireOp",EDGE,"E489"),sQuery(id+"F0.wireOp",EDGE,"E490"),sQuery(id+"F0.wireOp",EDGE,"E491"),sQuery(id+"F0.wireOp",EDGE,"E492"),sQuery(id+"F0.wireOp",EDGE,"E493"),sQuery(id+"F0.wireOp",EDGE,"E494"),sQuery(id+"F0.wireOp",EDGE,"E495"),sQuery(id+"F0.wireOp",EDGE,"E496"),sQuery(id+"F0.wireOp",EDGE,"E497"),sQuery(id+"F0.wireOp",EDGE,"E498"),sQuery(id+"F0.wireOp",EDGE,"E499"),sQuery(id+"F0.wireOp",EDGE,"E500"),sQuery(id+"F0.wireOp",EDGE,"E501"),sQuery(id+"F0.wireOp",EDGE,"E502"),sQuery(id+"F0.wireOp",EDGE,"E503"),sQuery(id+"F0.wireOp",EDGE,"E504"),sQuery(id+"F0.wireOp",EDGE,"E505"),sQuery(id+"F0.wireOp",EDGE,"E506"),sQuery(id+"F0.wireOp",EDGE,"E507"),sQuery(id+"F0.wireOp",EDGE,"E508"),sQuery(id+"F0.wireOp",EDGE,"E509"),sQuery(id+"F0.wireOp",EDGE,"E510"),sQuery(id+"F0.wireOp",EDGE,"E511")])],"isStart":false});
            var sketch = newSketch(context, id + "F2", { "sketchPlane" : qUnion([Q0])});
            skCircle(sketch, "E574", {"center": v(0, 38.1) * mm, "radius": 0.95 * mm});
            skCircle(sketch, "E575.1.0", {"center": v(-14.58, 35.2) * mm, "radius": 0.95 * mm});
            skCircle(sketch, "E575.2.0", {"center": v(-26.94, 26.94) * mm, "radius": 0.95 * mm});
            skCircle(sketch, "E575.3.0", {"center": v(-35.2, 14.58) * mm, "radius": 0.95 * mm});
            skCircle(sketch, "E575.4.0", {"center": v(-38.1, 0) * mm, "radius": 0.95 * mm});
            skCircle(sketch, "E575.5.0", {"center": v(-35.2, -14.58) * mm, "radius": 0.95 * mm});
            skCircle(sketch, "E575.6.0", {"center": v(-26.94, -26.94) * mm, "radius": 0.95 * mm});
            skCircle(sketch, "E575.7.0", {"center": v(-14.58, -35.2) * mm, "radius": 0.95 * mm});
            skCircle(sketch, "E575.8.0", {"center": v(0, -38.1) * mm, "radius": 0.95 * mm});
            skCircle(sketch, "E575.9.0", {"center": v(14.58, -35.2) * mm, "radius": 0.95 * mm});
            skCircle(sketch, "E575.10.0", {"center": v(26.94, -26.94) * mm, "radius": 0.95 * mm});
            skCircle(sketch, "E575.11.0", {"center": v(35.2, -14.58) * mm, "radius": 0.95 * mm});
            skCircle(sketch, "E575.12.0", {"center": v(38.1, 0) * mm, "radius": 0.95 * mm});
            skCircle(sketch, "E575.13.0", {"center": v(35.2, 14.58) * mm, "radius": 0.95 * mm});
            skCircle(sketch, "E575.14.0", {"center": v(26.94, 26.94) * mm, "radius": 0.95 * mm});
            skPoint(sketch, "E575.center", {"position": v(0, 0) * mm});
            skCircle(sketch, "E576.1.15.0", {"center": v(14.58, 35.2) * mm, "radius": 0.95 * mm});
            skSolve(sketch);
        }
        {
            var Q0;
            Q0 = qSketchRegion(id + "F2", true);
            extrude(context, id + "F3", {"entities" : qUnion([Q0]), "operationType" : NewBodyOperationType.REMOVE, "endBound" : BoundingType.THROUGH_ALL, "oppositeDirection" : true, "depth" : 25.4 * mm});
        }
        {
            var Q0;
            Q0=makeQuery(id+"F1.opExtrude","CAP_FACE",FACE,{"disambiguationData":[OSD([sQuery(id+"F0.wireOp",EDGE,"E16"),sQuery(id+"F0.wireOp",EDGE,"E17"),sQuery(id+"F0.wireOp",EDGE,"E18"),sQuery(id+"F0.wireOp",EDGE,"E19"),sQuery(id+"F0.wireOp",EDGE,"E20"),sQuery(id+"F0.wireOp",EDGE,"E21"),sQuery(id+"F0.wireOp",EDGE,"E22"),sQuery(id+"F0.wireOp",EDGE,"E23"),sQuery(id+"F0.wireOp",EDGE,"E24"),sQuery(id+"F0.wireOp",EDGE,"E26"),sQuery(id+"F0.wireOp",EDGE,"E27"),sQuery(id+"F0.wireOp",EDGE,"E28"),sQuery(id+"F0.wireOp",EDGE,"E29"),sQuery(id+"F0.wireOp",EDGE,"E30"),sQuery(id+"F0.wireOp",EDGE,"E31"),sQuery(id+"F0.wireOp",EDGE,"E32"),sQuery(id+"F0.wireOp",EDGE,"E33"),sQuery(id+"F0.wireOp",EDGE,"E34"),sQuery(id+"F0.wireOp",EDGE,"E35"),sQuery(id+"F0.wireOp",EDGE,"E36"),sQuery(id+"F0.wireOp",EDGE,"E37"),sQuery(id+"F0.wireOp",EDGE,"E38"),sQuery(id+"F0.wireOp",EDGE,"E39"),sQuery(id+"F0.wireOp",EDGE,"E40"),sQuery(id+"F0.wireOp",EDGE,"E41"),sQuery(id+"F0.wireOp",EDGE,"E42"),sQuery(id+"F0.wireOp",EDGE,"E61"),sQuery(id+"F0.wireOp",EDGE,"E62"),sQuery(id+"F0.wireOp",EDGE,"E63"),sQuery(id+"F0.wireOp",EDGE,"E64"),sQuery(id+"F0.wireOp",EDGE,"E65"),sQuery(id+"F0.wireOp",EDGE,"E66"),sQuery(id+"F0.wireOp",EDGE,"E67"),sQuery(id+"F0.wireOp",EDGE,"E68"),sQuery(id+"F0.wireOp",EDGE,"E69"),sQuery(id+"F0.wireOp",EDGE,"E70"),sQuery(id+"F0.wireOp",EDGE,"E71"),sQuery(id+"F0.wireOp",EDGE,"E72"),sQuery(id+"F0.wireOp",EDGE,"E73"),sQuery(id+"F0.wireOp",EDGE,"E74"),sQuery(id+"F0.wireOp",EDGE,"E75"),sQuery(id+"F0.wireOp",EDGE,"E76"),sQuery(id+"F0.wireOp",EDGE,"E77"),sQuery(id+"F0.wireOp",EDGE,"E78"),sQuery(id+"F0.wireOp",EDGE,"E79"),sQuery(id+"F0.wireOp",EDGE,"E80"),sQuery(id+"F0.wireOp",EDGE,"E81"),sQuery(id+"F0.wireOp",EDGE,"E82"),sQuery(id+"F0.wireOp",EDGE,"E83"),sQuery(id+"F0.wireOp",EDGE,"E84"),sQuery(id+"F0.wireOp",EDGE,"E85"),sQuery(id+"F0.wireOp",EDGE,"E86"),sQuery(id+"F0.wireOp",EDGE,"E87"),sQuery(id+"F0.wireOp",EDGE,"E106"),sQuery(id+"F0.wireOp",EDGE,"E107"),sQuery(id+"F0.wireOp",EDGE,"E108"),sQuery(id+"F0.wireOp",EDGE,"E109"),sQuery(id+"F0.wireOp",EDGE,"E110"),sQuery(id+"F0.wireOp",EDGE,"E111"),sQuery(id+"F0.wireOp",EDGE,"E112"),sQuery(id+"F0.wireOp",EDGE,"E113"),sQuery(id+"F0.wireOp",EDGE,"E114"),sQuery(id+"F0.wireOp",EDGE,"E115"),sQuery(id+"F0.wireOp",EDGE,"E116"),sQuery(id+"F0.wireOp",EDGE,"E117"),sQuery(id+"F0.wireOp",EDGE,"E118"),sQuery(id+"F0.wireOp",EDGE,"E119"),sQuery(id+"F0.wireOp",EDGE,"E120"),sQuery(id+"F0.wireOp",EDGE,"E121"),sQuery(id+"F0.wireOp",EDGE,"E122"),sQuery(id+"F0.wireOp",EDGE,"E123"),sQuery(id+"F0.wireOp",EDGE,"E124"),sQuery(id+"F0.wireOp",EDGE,"E125"),sQuery(id+"F0.wireOp",EDGE,"E126"),sQuery(id+"F0.wireOp",EDGE,"E127"),sQuery(id+"F0.wireOp",EDGE,"E128"),sQuery(id+"F0.wireOp",EDGE,"E129"),sQuery(id+"F0.wireOp",EDGE,"E130"),sQuery(id+"F0.wireOp",EDGE,"E131"),sQuery(id+"F0.wireOp",EDGE,"E132"),sQuery(id+"F0.wireOp",EDGE,"E169"),sQuery(id+"F0.wireOp",EDGE,"E170"),sQuery(id+"F0.wireOp",EDGE,"E151"),sQuery(id+"F0.wireOp",EDGE,"E152"),sQuery(id+"F0.wireOp",EDGE,"E153"),sQuery(id+"F0.wireOp",EDGE,"E154"),sQuery(id+"F0.wireOp",EDGE,"E155"),sQuery(id+"F0.wireOp",EDGE,"E156"),sQuery(id+"F0.wireOp",EDGE,"E157"),sQuery(id+"F0.wireOp",EDGE,"E158"),sQuery(id+"F0.wireOp",EDGE,"E159"),sQuery(id+"F0.wireOp",EDGE,"E160"),sQuery(id+"F0.wireOp",EDGE,"E161"),sQuery(id+"F0.wireOp",EDGE,"E162"),sQuery(id+"F0.wireOp",EDGE,"E163"),sQuery(id+"F0.wireOp",EDGE,"E164"),sQuery(id+"F0.wireOp",EDGE,"E165"),sQuery(id+"F0.wireOp",EDGE,"E166"),sQuery(id+"F0.wireOp",EDGE,"E167"),sQuery(id+"F0.wireOp",EDGE,"E168"),sQuery(id+"F0.wireOp",EDGE,"E171"),sQuery(id+"F0.wireOp",EDGE,"E172"),sQuery(id+"F0.wireOp",EDGE,"E173"),sQuery(id+"F0.wireOp",EDGE,"E174"),sQuery(id+"F0.wireOp",EDGE,"E175"),sQuery(id+"F0.wireOp",EDGE,"E176"),sQuery(id+"F0.wireOp",EDGE,"E177"),sQuery(id+"F0.wireOp",EDGE,"E196"),sQuery(id+"F0.wireOp",EDGE,"E197"),sQuery(id+"F0.wireOp",EDGE,"E198"),sQuery(id+"F0.wireOp",EDGE,"E199"),sQuery(id+"F0.wireOp",EDGE,"E200"),sQuery(id+"F0.wireOp",EDGE,"E201"),sQuery(id+"F0.wireOp",EDGE,"E202"),sQuery(id+"F0.wireOp",EDGE,"E203"),sQuery(id+"F0.wireOp",EDGE,"E204"),sQuery(id+"F0.wireOp",EDGE,"E205"),sQuery(id+"F0.wireOp",EDGE,"E206"),sQuery(id+"F0.wireOp",EDGE,"E207"),sQuery(id+"F0.wireOp",EDGE,"E208"),sQuery(id+"F0.wireOp",EDGE,"E209"),sQuery(id+"F0.wireOp",EDGE,"E210"),sQuery(id+"F0.wireOp",EDGE,"E211"),sQuery(id+"F0.wireOp",EDGE,"E212"),sQuery(id+"F0.wireOp",EDGE,"E213"),sQuery(id+"F0.wireOp",EDGE,"E214"),sQuery(id+"F0.wireOp",EDGE,"E215"),sQuery(id+"F0.wireOp",EDGE,"E216"),sQuery(id+"F0.wireOp",EDGE,"E217"),sQuery(id+"F0.wireOp",EDGE,"E218"),sQuery(id+"F0.wireOp",EDGE,"E219"),sQuery(id+"F0.wireOp",EDGE,"E220"),sQuery(id+"F0.wireOp",EDGE,"E221"),sQuery(id+"F0.wireOp",EDGE,"E222"),sQuery(id+"F0.wireOp",EDGE,"E241"),sQuery(id+"F0.wireOp",EDGE,"E242"),sQuery(id+"F0.wireOp",EDGE,"E243"),sQuery(id+"F0.wireOp",EDGE,"E244"),sQuery(id+"F0.wireOp",EDGE,"E245"),sQuery(id+"F0.wireOp",EDGE,"E246"),sQuery(id+"F0.wireOp",EDGE,"E247"),sQuery(id+"F0.wireOp",EDGE,"E248"),sQuery(id+"F0.wireOp",EDGE,"E249"),sQuery(id+"F0.wireOp",EDGE,"E250"),sQuery(id+"F0.wireOp",EDGE,"E251"),sQuery(id+"F0.wireOp",EDGE,"E252"),sQuery(id+"F0.wireOp",EDGE,"E253"),sQuery(id+"F0.wireOp",EDGE,"E254"),sQuery(id+"F0.wireOp",EDGE,"E255"),sQuery(id+"F0.wireOp",EDGE,"E256"),sQuery(id+"F0.wireOp",EDGE,"E257"),sQuery(id+"F0.wireOp",EDGE,"E258"),sQuery(id+"F0.wireOp",EDGE,"E259"),sQuery(id+"F0.wireOp",EDGE,"E260"),sQuery(id+"F0.wireOp",EDGE,"E261"),sQuery(id+"F0.wireOp",EDGE,"E262"),sQuery(id+"F0.wireOp",EDGE,"E263"),sQuery(id+"F0.wireOp",EDGE,"E264"),sQuery(id+"F0.wireOp",EDGE,"E265"),sQuery(id+"F0.wireOp",EDGE,"E266"),sQuery(id+"F0.wireOp",EDGE,"E267"),sQuery(id+"F0.wireOp",EDGE,"E286"),sQuery(id+"F0.wireOp",EDGE,"E287"),sQuery(id+"F0.wireOp",EDGE,"E288"),sQuery(id+"F0.wireOp",EDGE,"E289"),sQuery(id+"F0.wireOp",EDGE,"E290"),sQuery(id+"F0.wireOp",EDGE,"E291"),sQuery(id+"F0.wireOp",EDGE,"E292"),sQuery(id+"F0.wireOp",EDGE,"E293"),sQuery(id+"F0.wireOp",EDGE,"E294"),sQuery(id+"F0.wireOp",EDGE,"E295"),sQuery(id+"F0.wireOp",EDGE,"E296"),sQuery(id+"F0.wireOp",EDGE,"E297"),sQuery(id+"F0.wireOp",EDGE,"E298"),sQuery(id+"F0.wireOp",EDGE,"E299"),sQuery(id+"F0.wireOp",EDGE,"E300"),sQuery(id+"F0.wireOp",EDGE,"E301"),sQuery(id+"F0.wireOp",EDGE,"E302"),sQuery(id+"F0.wireOp",EDGE,"E303"),sQuery(id+"F0.wireOp",EDGE,"E304"),sQuery(id+"F0.wireOp",EDGE,"E305"),sQuery(id+"F0.wireOp",EDGE,"E306"),sQuery(id+"F0.wireOp",EDGE,"E307"),sQuery(id+"F0.wireOp",EDGE,"E308"),sQuery(id+"F0.wireOp",EDGE,"E309"),sQuery(id+"F0.wireOp",EDGE,"E310"),sQuery(id+"F0.wireOp",EDGE,"E311"),sQuery(id+"F0.wireOp",EDGE,"E312"),sQuery(id+"F0.wireOp",EDGE,"E347"),sQuery(id+"F0.wireOp",EDGE,"E348"),sQuery(id+"F0.wireOp",EDGE,"E349"),sQuery(id+"F0.wireOp",EDGE,"E350"),sQuery(id+"F0.wireOp",EDGE,"E351"),sQuery(id+"F0.wireOp",EDGE,"E352"),sQuery(id+"F0.wireOp",EDGE,"E353"),sQuery(id+"F0.wireOp",EDGE,"E354"),sQuery(id+"F0.wireOp",EDGE,"E355"),sQuery(id+"F0.wireOp",EDGE,"E356"),sQuery(id+"F0.wireOp",EDGE,"E357"),sQuery(id+"F0.wireOp",EDGE,"E358"),sQuery(id+"F0.wireOp",EDGE,"E359"),sQuery(id+"F0.wireOp",EDGE,"E360"),sQuery(id+"F0.wireOp",EDGE,"E361"),sQuery(id+"F0.wireOp",EDGE,"E362"),sQuery(id+"F0.wireOp",EDGE,"E363"),sQuery(id+"F0.wireOp",EDGE,"E364"),sQuery(id+"F0.wireOp",EDGE,"E365"),sQuery(id+"F0.wireOp",EDGE,"E366"),sQuery(id+"F0.wireOp",EDGE,"E367"),sQuery(id+"F0.wireOp",EDGE,"E368"),sQuery(id+"F0.wireOp",EDGE,"E369"),sQuery(id+"F0.wireOp",EDGE,"E370"),sQuery(id+"F0.wireOp",EDGE,"E371"),sQuery(id+"F0.wireOp",EDGE,"E372"),sQuery(id+"F0.wireOp",EDGE,"E373"),sQuery(id+"F0.wireOp",EDGE,"E376"),sQuery(id+"F0.wireOp",EDGE,"E377"),sQuery(id+"F0.wireOp",EDGE,"E378"),sQuery(id+"F0.wireOp",EDGE,"E379"),sQuery(id+"F0.wireOp",EDGE,"E380"),sQuery(id+"F0.wireOp",EDGE,"E381"),sQuery(id+"F0.wireOp",EDGE,"E382"),sQuery(id+"F0.wireOp",EDGE,"E383"),sQuery(id+"F0.wireOp",EDGE,"E384"),sQuery(id+"F0.wireOp",EDGE,"E385"),sQuery(id+"F0.wireOp",EDGE,"E386"),sQuery(id+"F0.wireOp",EDGE,"E387"),sQuery(id+"F0.wireOp",EDGE,"E388"),sQuery(id+"F0.wireOp",EDGE,"E389"),sQuery(id+"F0.wireOp",EDGE,"E390"),sQuery(id+"F0.wireOp",EDGE,"E391"),sQuery(id+"F0.wireOp",EDGE,"E392"),sQuery(id+"F0.wireOp",EDGE,"E393"),sQuery(id+"F0.wireOp",EDGE,"E394"),sQuery(id+"F0.wireOp",EDGE,"E395"),sQuery(id+"F0.wireOp",EDGE,"E396"),sQuery(id+"F0.wireOp",EDGE,"E397"),sQuery(id+"F0.wireOp",EDGE,"E398"),sQuery(id+"F0.wireOp",EDGE,"E399"),sQuery(id+"F0.wireOp",EDGE,"E400"),sQuery(id+"F0.wireOp",EDGE,"E401"),sQuery(id+"F0.wireOp",EDGE,"E402"),sQuery(id+"F0.wireOp",EDGE,"E403"),sQuery(id+"F0.wireOp",EDGE,"E404"),sQuery(id+"F0.wireOp",EDGE,"E405"),sQuery(id+"F0.wireOp",EDGE,"E406"),sQuery(id+"F0.wireOp",EDGE,"E407"),sQuery(id+"F0.wireOp",EDGE,"E408"),sQuery(id+"F0.wireOp",EDGE,"E409"),sQuery(id+"F0.wireOp",EDGE,"E410"),sQuery(id+"F0.wireOp",EDGE,"E411"),sQuery(id+"F0.wireOp",EDGE,"E412"),sQuery(id+"F0.wireOp",EDGE,"E413"),sQuery(id+"F0.wireOp",EDGE,"E414"),sQuery(id+"F0.wireOp",EDGE,"E415"),sQuery(id+"F0.wireOp",EDGE,"E416"),sQuery(id+"F0.wireOp",EDGE,"E417"),sQuery(id+"F0.wireOp",EDGE,"E418"),sQuery(id+"F0.wireOp",EDGE,"E419"),sQuery(id+"F0.wireOp",EDGE,"E420"),sQuery(id+"F0.wireOp",EDGE,"E421"),sQuery(id+"F0.wireOp",EDGE,"E422"),sQuery(id+"F0.wireOp",EDGE,"E423"),sQuery(id+"F0.wireOp",EDGE,"E424"),sQuery(id+"F0.wireOp",EDGE,"E425"),sQuery(id+"F0.wireOp",EDGE,"E426"),sQuery(id+"F0.wireOp",EDGE,"E427"),sQuery(id+"F0.wireOp",EDGE,"E428"),sQuery(id+"F0.wireOp",EDGE,"E429"),sQuery(id+"F0.wireOp",EDGE,"E430"),sQuery(id+"F0.wireOp",EDGE,"E431"),sQuery(id+"F0.wireOp",EDGE,"E432"),sQuery(id+"F0.wireOp",EDGE,"E433"),sQuery(id+"F0.wireOp",EDGE,"E434"),sQuery(id+"F0.wireOp",EDGE,"E435"),sQuery(id+"F0.wireOp",EDGE,"E436"),sQuery(id+"F0.wireOp",EDGE,"E437"),sQuery(id+"F0.wireOp",EDGE,"E438"),sQuery(id+"F0.wireOp",EDGE,"E439"),sQuery(id+"F0.wireOp",EDGE,"E480"),sQuery(id+"F0.wireOp",EDGE,"E481"),sQuery(id+"F0.wireOp",EDGE,"E482"),sQuery(id+"F0.wireOp",EDGE,"E483"),sQuery(id+"F0.wireOp",EDGE,"E484"),sQuery(id+"F0.wireOp",EDGE,"E485"),sQuery(id+"F0.wireOp",EDGE,"E486"),sQuery(id+"F0.wireOp",EDGE,"E487"),sQuery(id+"F0.wireOp",EDGE,"E488"),sQuery(id+"F0.wireOp",EDGE,"E489"),sQuery(id+"F0.wireOp",EDGE,"E490"),sQuery(id+"F0.wireOp",EDGE,"E491"),sQuery(id+"F0.wireOp",EDGE,"E492"),sQuery(id+"F0.wireOp",EDGE,"E493"),sQuery(id+"F0.wireOp",EDGE,"E494"),sQuery(id+"F0.wireOp",EDGE,"E495"),sQuery(id+"F0.wireOp",EDGE,"E496"),sQuery(id+"F0.wireOp",EDGE,"E497"),sQuery(id+"F0.wireOp",EDGE,"E498"),sQuery(id+"F0.wireOp",EDGE,"E499"),sQuery(id+"F0.wireOp",EDGE,"E500"),sQuery(id+"F0.wireOp",EDGE,"E501"),sQuery(id+"F0.wireOp",EDGE,"E502"),sQuery(id+"F0.wireOp",EDGE,"E503"),sQuery(id+"F0.wireOp",EDGE,"E504"),sQuery(id+"F0.wireOp",EDGE,"E505"),sQuery(id+"F0.wireOp",EDGE,"E506"),sQuery(id+"F0.wireOp",EDGE,"E507"),sQuery(id+"F0.wireOp",EDGE,"E508"),sQuery(id+"F0.wireOp",EDGE,"E509"),sQuery(id+"F0.wireOp",EDGE,"E510"),sQuery(id+"F0.wireOp",EDGE,"E511")])],"isStart":false});
            var sketch = newSketch(context, id + "F4", { "sketchPlane" : qUnion([Q0])});
            skEllipse(sketch, "E577", {"center": v(-13.84, 15.88) * mm, "majorRadius": 11.43 * mm, "minorRadius": 7.62 * mm, "majorAxis": v(0.56, -0.83)});
            skEllipse(sketch, "E578.1.0", {"center": v(-20.81, 3.27) * mm, "majorRadius": 11.43 * mm, "minorRadius": 7.62 * mm, "majorAxis": v(0.96, -0.28)});
            skEllipse(sketch, "E578.2.0", {"center": v(-18.05, -10.87) * mm, "majorRadius": 11.43 * mm, "minorRadius": 7.62 * mm, "majorAxis": v(0.91, 0.4)});
            skEllipse(sketch, "E578.3.0", {"center": v(-6.84, -19.93) * mm, "majorRadius": 11.43 * mm, "minorRadius": 7.62 * mm, "majorAxis": v(0.44, 0.9)});
            skEllipse(sketch, "E578.4.0", {"center": v(7.57, -19.66) * mm, "majorRadius": 11.43 * mm, "minorRadius": 7.62 * mm, "majorAxis": v(-0.24, 0.97)});
            skEllipse(sketch, "E578.5.0", {"center": v(18.44, -10.2) * mm, "majorRadius": 11.43 * mm, "minorRadius": 7.62 * mm, "majorAxis": v(-0.8, 0.59)});
            skEllipse(sketch, "E578.6.0", {"center": v(20.68, 4.04) * mm, "majorRadius": 11.43 * mm, "minorRadius": 7.62 * mm, "majorAxis": v(-1, -0.07)});
            skEllipse(sketch, "E578.7.0", {"center": v(13.24, 16.39) * mm, "majorRadius": 11.43 * mm, "minorRadius": 7.62 * mm, "majorAxis": v(-0.72, -0.7)});
            skEllipse(sketch, "E578.8.0", {"center": v(-0.4, 21.06) * mm, "majorRadius": 11.43 * mm, "minorRadius": 7.62 * mm, "majorAxis": v(-0.1, -1)});
            skPoint(sketch, "E578.center", {"position": v(0, 0) * mm});
            skCircle(sketch, "E579", {"center": v(0, 0) * mm, "radius": 10.16 * mm});
            skCircle(sketch, "E580", {"center": v(-2.2, 26.74) * mm, "radius": 0.95 * mm});
            skCircle(sketch, "E581.0.1.0", {"center": v(-2.2, 22.93) * mm, "radius": 0.95 * mm});
            skCircle(sketch, "E581.0.2.0", {"center": v(-2.2, 19.12) * mm, "radius": 0.95 * mm});
            skCircle(sketch, "E581.0.3.0", {"center": v(-2.2, 15.3) * mm, "radius": 0.95 * mm});
            skCircle(sketch, "E581.1.0.0", {"center": v(1.62, 26.74) * mm, "radius": 0.95 * mm});
            skCircle(sketch, "E581.1.1.0", {"center": v(1.62, 22.93) * mm, "radius": 0.95 * mm});
            skCircle(sketch, "E581.1.2.0", {"center": v(1.62, 19.12) * mm, "radius": 0.95 * mm});
            skCircle(sketch, "E581.1.3.0", {"center": v(1.62, 15.3) * mm, "radius": 0.95 * mm});
            skLineSegment(sketch, "E581.direction1", {"start": v(-2.2, 26.74) * mm, "end": v(1.62, 26.74) * mm, "construction": true});
            skLineSegment(sketch, "E581.direction2", {"start": v(-2.2, 26.74) * mm, "end": v(-2.2, 22.93) * mm, "construction": true});
            skCircle(sketch, "E582.1.0", {"center": v(-18.87, 19.07) * mm, "radius": 0.95 * mm});
            skCircle(sketch, "E582.1.1", {"center": v(-15.95, 21.52) * mm, "radius": 0.95 * mm});
            skCircle(sketch, "E582.1.2", {"center": v(-13.5, 18.6) * mm, "radius": 0.95 * mm});
            skCircle(sketch, "E582.1.3", {"center": v(-16.42, 16.15) * mm, "radius": 0.95 * mm});
            skCircle(sketch, "E582.1.4", {"center": v(-13.97, 13.23) * mm, "radius": 0.95 * mm});
            skCircle(sketch, "E582.1.5", {"center": v(-11.05, 15.68) * mm, "radius": 0.95 * mm});
            skCircle(sketch, "E582.1.6", {"center": v(-11.52, 10.32) * mm, "radius": 0.95 * mm});
            skCircle(sketch, "E582.1.7", {"center": v(-8.6, 12.76) * mm, "radius": 0.95 * mm});
            skCircle(sketch, "E582.2.0", {"center": v(-26.71, 2.48) * mm, "radius": 0.95 * mm});
            skCircle(sketch, "E582.2.1", {"center": v(-26.05, 6.23) * mm, "radius": 0.95 * mm});
            skCircle(sketch, "E582.2.2", {"center": v(-22.3, 5.57) * mm, "radius": 0.95 * mm});
            skCircle(sketch, "E582.2.3", {"center": v(-22.96, 1.82) * mm, "radius": 0.95 * mm});
            skCircle(sketch, "E582.2.4", {"center": v(-19.2, 1.16) * mm, "radius": 0.95 * mm});
            skCircle(sketch, "E582.2.5", {"center": v(-18.55, 4.91) * mm, "radius": 0.95 * mm});
            skCircle(sketch, "E582.2.6", {"center": v(-15.46, 0.5) * mm, "radius": 0.95 * mm});
            skCircle(sketch, "E582.2.7", {"center": v(-14.8, 4.25) * mm, "radius": 0.95 * mm});
            skCircle(sketch, "E582.3.0", {"center": v(-22.06, -15.27) * mm, "radius": 0.95 * mm});
            skCircle(sketch, "E582.3.1", {"center": v(-23.96, -11.97) * mm, "radius": 0.95 * mm});
            skCircle(sketch, "E582.3.2", {"center": v(-20.66, -10.06) * mm, "radius": 0.95 * mm});
            skCircle(sketch, "E582.3.3", {"center": v(-18.76, -13.36) * mm, "radius": 0.95 * mm});
            skCircle(sketch, "E582.3.4", {"center": v(-15.46, -11.46) * mm, "radius": 0.95 * mm});
            skCircle(sketch, "E582.3.5", {"center": v(-17.36, -8.16) * mm, "radius": 0.95 * mm});
            skCircle(sketch, "E582.3.6", {"center": v(-12.16, -9.55) * mm, "radius": 0.95 * mm});
            skCircle(sketch, "E582.3.7", {"center": v(-14.06, -6.25) * mm, "radius": 0.95 * mm});
            skCircle(sketch, "E582.4.0", {"center": v(-7.08, -25.88) * mm, "radius": 0.95 * mm});
            skCircle(sketch, "E582.4.1", {"center": v(-10.66, -24.57) * mm, "radius": 0.95 * mm});
            skCircle(sketch, "E582.4.2", {"center": v(-9.36, -21) * mm, "radius": 0.95 * mm});
            skCircle(sketch, "E582.4.3", {"center": v(-5.78, -22.3) * mm, "radius": 0.95 * mm});
            skCircle(sketch, "E582.4.4", {"center": v(-4.48, -18.71) * mm, "radius": 0.95 * mm});
            skCircle(sketch, "E582.4.5", {"center": v(-8.06, -17.41) * mm, "radius": 0.95 * mm});
            skCircle(sketch, "E582.4.6", {"center": v(-3.17, -15.13) * mm, "radius": 0.95 * mm});
            skCircle(sketch, "E582.4.7", {"center": v(-6.75, -13.83) * mm, "radius": 0.95 * mm});
            skCircle(sketch, "E582.5.0", {"center": v(11.2, -24.37) * mm, "radius": 0.95 * mm});
            skCircle(sketch, "E582.5.1", {"center": v(7.63, -25.68) * mm, "radius": 0.95 * mm});
            skCircle(sketch, "E582.5.2", {"center": v(6.32, -22.1) * mm, "radius": 0.95 * mm});
            skCircle(sketch, "E582.5.3", {"center": v(9.9, -20.8) * mm, "radius": 0.95 * mm});
            skCircle(sketch, "E582.5.4", {"center": v(8.6, -17.21) * mm, "radius": 0.95 * mm});
            skCircle(sketch, "E582.5.5", {"center": v(5.02, -18.52) * mm, "radius": 0.95 * mm});
            skCircle(sketch, "E582.5.6", {"center": v(7.3, -13.63) * mm, "radius": 0.95 * mm});
            skCircle(sketch, "E582.5.7", {"center": v(3.72, -14.94) * mm, "radius": 0.95 * mm});
            skCircle(sketch, "E582.6.0", {"center": v(24.25, -11.47) * mm, "radius": 0.95 * mm});
            skCircle(sketch, "E582.6.1", {"center": v(22.35, -14.77) * mm, "radius": 0.95 * mm});
            skCircle(sketch, "E582.6.2", {"center": v(19.05, -12.86) * mm, "radius": 0.95 * mm});
            skCircle(sketch, "E582.6.3", {"center": v(20.95, -9.56) * mm, "radius": 0.95 * mm});
            skCircle(sketch, "E582.6.4", {"center": v(17.65, -7.66) * mm, "radius": 0.95 * mm});
            skCircle(sketch, "E582.6.5", {"center": v(15.75, -10.96) * mm, "radius": 0.95 * mm});
            skCircle(sketch, "E582.6.6", {"center": v(14.35, -5.75) * mm, "radius": 0.95 * mm});
            skCircle(sketch, "E582.6.7", {"center": v(12.45, -9.05) * mm, "radius": 0.95 * mm});
            skCircle(sketch, "E582.7.0", {"center": v(25.95, 6.8) * mm, "radius": 0.95 * mm});
            skCircle(sketch, "E582.7.1", {"center": v(26.61, 3.05) * mm, "radius": 0.95 * mm});
            skCircle(sketch, "E582.7.2", {"center": v(22.86, 2.39) * mm, "radius": 0.95 * mm});
            skCircle(sketch, "E582.7.3", {"center": v(22.2, 6.14) * mm, "radius": 0.95 * mm});
            skCircle(sketch, "E582.7.4", {"center": v(18.45, 5.48) * mm, "radius": 0.95 * mm});
            skCircle(sketch, "E582.7.5", {"center": v(19.1, 1.73) * mm, "radius": 0.95 * mm});
            skCircle(sketch, "E582.7.6", {"center": v(14.7, 4.82) * mm, "radius": 0.95 * mm});
            skCircle(sketch, "E582.7.7", {"center": v(15.36, 1.07) * mm, "radius": 0.95 * mm});
            skCircle(sketch, "E582.8.0", {"center": v(15.5, 21.9) * mm, "radius": 0.95 * mm});
            skCircle(sketch, "E582.8.1", {"center": v(18.42, 19.44) * mm, "radius": 0.95 * mm});
            skCircle(sketch, "E582.8.2", {"center": v(15.98, 16.52) * mm, "radius": 0.95 * mm});
            skCircle(sketch, "E582.8.3", {"center": v(13.06, 18.97) * mm, "radius": 0.95 * mm});
            skCircle(sketch, "E582.8.4", {"center": v(10.6, 16.06) * mm, "radius": 0.95 * mm});
            skCircle(sketch, "E582.8.5", {"center": v(13.53, 13.6) * mm, "radius": 0.95 * mm});
            skCircle(sketch, "E582.8.6", {"center": v(8.16, 13.14) * mm, "radius": 0.95 * mm});
            skCircle(sketch, "E582.8.7", {"center": v(11.08, 10.69) * mm, "radius": 0.95 * mm});
            skSolve(sketch);
        }
        {
            var Q0;
            Q0 = qSketchRegion(id + "F4", true);
            var Q1;
            {var subQ0=sQuery(id+"F4.wireOp",EDGE,"E579");var subQ17=sQuery(id+"F4.wireOp",EDGE,"E577");var subQ18=makeQuery(id+"F4.imprint","INTERSECT",VERTEX,{"disambiguationData":[OD(0.0)],"derivedFrom":[subQ17,subQ0]});Q1=makeQuery(id+"F4.imprint","IMPRINT",FACE,{"disambiguationData":[TD([[makeQuery(id+"F4.imprint","IMPRINT",EDGE,{"disambiguationData":[TD([[subQ18,1.0]])],"derivedFrom":subQ17}),-1.0]])]});}
            var Q2;
            {var subQ0=sQuery(id+"F4.wireOp",EDGE,"E579");var subQ1=sQuery(id+"F4.wireOp",EDGE,"E578.1.0");var subQ2=makeQuery(id+"F4.imprint","INTERSECT",VERTEX,{"disambiguationData":[OD(0.0)],"derivedFrom":[subQ1,subQ0]});Q2=makeQuery(id+"F4.imprint","IMPRINT",FACE,{"disambiguationData":[TD([[makeQuery(id+"F4.imprint","IMPRINT",EDGE,{"disambiguationData":[TD([[subQ2,1.0]])],"derivedFrom":subQ1}),1.0]])]});}
            var Q3;
            {var subQ0=sQuery(id+"F4.wireOp",EDGE,"E579");var subQ1=sQuery(id+"F4.wireOp",EDGE,"E578.3.0");var subQ2=makeQuery(id+"F4.imprint","INTERSECT",VERTEX,{"disambiguationData":[OD(0.0)],"derivedFrom":[subQ1,subQ0]});Q3=makeQuery(id+"F4.imprint","IMPRINT",FACE,{"disambiguationData":[TD([[makeQuery(id+"F4.imprint","IMPRINT",EDGE,{"disambiguationData":[TD([[subQ2,1.0]])],"derivedFrom":subQ1}),1.0]])]});}
            var Q4;
            {var subQ0=sQuery(id+"F4.wireOp",EDGE,"E579");var subQ1=sQuery(id+"F4.wireOp",EDGE,"E578.2.0");var subQ2=makeQuery(id+"F4.imprint","INTERSECT",VERTEX,{"disambiguationData":[OD(0.0)],"derivedFrom":[subQ1,subQ0]});Q4=makeQuery(id+"F4.imprint","IMPRINT",FACE,{"disambiguationData":[TD([[makeQuery(id+"F4.imprint","IMPRINT",EDGE,{"disambiguationData":[TD([[subQ2,1.0]])],"derivedFrom":subQ1}),1.0]])]});}
            var Q5;
            {var subQ0=sQuery(id+"F4.wireOp",EDGE,"E579");var subQ1=sQuery(id+"F4.wireOp",EDGE,"E578.4.0");var subQ2=makeQuery(id+"F4.imprint","INTERSECT",VERTEX,{"disambiguationData":[OD(0.0)],"derivedFrom":[subQ1,subQ0]});Q5=makeQuery(id+"F4.imprint","IMPRINT",FACE,{"disambiguationData":[TD([[makeQuery(id+"F4.imprint","IMPRINT",EDGE,{"disambiguationData":[TD([[subQ2,1.0]])],"derivedFrom":subQ1}),1.0]])]});}
            var Q6;
            {var subQ0=sQuery(id+"F4.wireOp",EDGE,"E579");var subQ1=sQuery(id+"F4.wireOp",EDGE,"E578.5.0");var subQ2=makeQuery(id+"F4.imprint","INTERSECT",VERTEX,{"disambiguationData":[OD(0.0)],"derivedFrom":[subQ1,subQ0]});Q6=makeQuery(id+"F4.imprint","IMPRINT",FACE,{"disambiguationData":[TD([[makeQuery(id+"F4.imprint","IMPRINT",EDGE,{"disambiguationData":[TD([[subQ2,1.0]])],"derivedFrom":subQ1}),1.0]])]});}
            var Q7;
            {var subQ0=sQuery(id+"F4.wireOp",EDGE,"E579");var subQ1=sQuery(id+"F4.wireOp",EDGE,"E578.6.0");var subQ2=makeQuery(id+"F4.imprint","INTERSECT",VERTEX,{"disambiguationData":[OD(0.0)],"derivedFrom":[subQ1,subQ0]});Q7=makeQuery(id+"F4.imprint","IMPRINT",FACE,{"disambiguationData":[TD([[makeQuery(id+"F4.imprint","IMPRINT",EDGE,{"disambiguationData":[TD([[subQ2,1.0]])],"derivedFrom":subQ1}),1.0]])]});}
            var Q8;
            {var subQ0=sQuery(id+"F4.wireOp",EDGE,"E579");var subQ1=sQuery(id+"F4.wireOp",EDGE,"E578.7.0");var subQ2=makeQuery(id+"F4.imprint","INTERSECT",VERTEX,{"disambiguationData":[OD(0.0)],"derivedFrom":[subQ1,subQ0]});Q8=makeQuery(id+"F4.imprint","IMPRINT",FACE,{"disambiguationData":[TD([[makeQuery(id+"F4.imprint","IMPRINT",EDGE,{"disambiguationData":[TD([[subQ2,1.0]])],"derivedFrom":subQ1}),1.0]])]});}
            var Q9;
            {var subQ0=sQuery(id+"F4.wireOp",EDGE,"E579");var subQ1=sQuery(id+"F4.wireOp",EDGE,"E578.8.0");var subQ2=makeQuery(id+"F4.imprint","INTERSECT",VERTEX,{"disambiguationData":[OD(0.0)],"derivedFrom":[subQ1,subQ0]});Q9=makeQuery(id+"F4.imprint","IMPRINT",FACE,{"disambiguationData":[TD([[makeQuery(id+"F4.imprint","IMPRINT",EDGE,{"disambiguationData":[TD([[subQ2,1.0]])],"derivedFrom":subQ1}),1.0]])]});}
            var Q10;
            {var subQ0=sQuery(id+"F4.wireOp",EDGE,"E579");var subQ1=sQuery(id+"F4.wireOp",EDGE,"E577");var subQ2=makeQuery(id+"F4.imprint","INTERSECT",VERTEX,{"disambiguationData":[OD(0.0)],"derivedFrom":[subQ1,subQ0]});Q10=makeQuery(id+"F4.imprint","IMPRINT",FACE,{"disambiguationData":[TD([[makeQuery(id+"F4.imprint","IMPRINT",EDGE,{"disambiguationData":[TD([[subQ2,1.0]])],"derivedFrom":subQ1}),1.0]])]});}
            extrude(context, id + "F5", {"entities" : qUnion([Q0, Q1, Q2, Q3, Q4, Q5, Q6, Q7, Q8, Q9, Q10]), "operationType" : NewBodyOperationType.ADD, "oppositeDirection" : true, "depth" : 3.17 * mm});
        }
        {
            var Q0;
            Q0=qSketchRegion(id+"F0",true);
            var Q1;
            {var subQ6=sQuery(id+"F0.wireOp",EDGE,"E1");Q1=makeQuery(id+"F0.imprint","IMPRINT",FACE,{"disambiguationData":[TD([[makeQuery(id+"F0.imprint","IMPRINT",EDGE,{"derivedFrom":subQ6}),-1.0]])]});}
            var Q2;
            {var subQ83=sQuery(id+"F0.wireOp",EDGE,"E441");Q2=makeQuery(id+"F0.imprint","IMPRINT",FACE,{"disambiguationData":[TD([[makeQuery(id+"F0.imprint","IMPRINT",EDGE,{"derivedFrom":subQ83}),1.0]])]});}
            var Q3;
            {var subQ1=sQuery(id+"F0.wireOp",EDGE,"E5");Q3=makeQuery(id+"F0.imprint","IMPRINT",FACE,{"disambiguationData":[TD([[makeQuery(id+"F0.imprint","IMPRINT",EDGE,{"derivedFrom":subQ1}),-1.0]])]});}
            var Q4;
            {var subQ19=sQuery(id+"F0.wireOp",EDGE,"E544");Q4=makeQuery(id+"F0.imprint","IMPRINT",FACE,{"disambiguationData":[TD([[makeQuery(id+"F0.imprint","IMPRINT",EDGE,{"derivedFrom":subQ19}),1.0]])]});}
            var Q5;
            {var subQ12=sQuery(id+"F0.wireOp",EDGE,"E226");Q5=makeQuery(id+"F0.imprint","IMPRINT",FACE,{"disambiguationData":[TD([[makeQuery(id+"F0.imprint","IMPRINT",EDGE,{"derivedFrom":subQ12}),-1.0]])]});}
            var Q6;
            {var subQ4=sQuery(id+"F0.wireOp",EDGE,"E230");Q6=makeQuery(id+"F0.imprint","IMPRINT",FACE,{"disambiguationData":[TD([[makeQuery(id+"F0.imprint","IMPRINT",EDGE,{"derivedFrom":subQ4}),-1.0]])]});}
            var Q7;
            {var subQ10=sQuery(id+"F0.wireOp",EDGE,"E181");Q7=makeQuery(id+"F0.imprint","IMPRINT",FACE,{"disambiguationData":[TD([[makeQuery(id+"F0.imprint","IMPRINT",EDGE,{"derivedFrom":subQ10}),-1.0]])]});}
            var Q8;
            {var subQ10=sQuery(id+"F0.wireOp",EDGE,"E91");Q8=makeQuery(id+"F0.imprint","IMPRINT",FACE,{"disambiguationData":[TD([[makeQuery(id+"F0.imprint","IMPRINT",EDGE,{"derivedFrom":subQ10}),-1.0]])]});}
            var Q9;
            {var subQ1=sQuery(id+"F0.wireOp",EDGE,"E271");Q9=makeQuery(id+"F0.imprint","IMPRINT",FACE,{"disambiguationData":[TD([[makeQuery(id+"F0.imprint","IMPRINT",EDGE,{"derivedFrom":subQ1}),-1.0]])]});}
            var Q10;
            {var subQ6=sQuery(id+"F0.wireOp",EDGE,"E332");Q10=makeQuery(id+"F0.imprint","IMPRINT",FACE,{"disambiguationData":[TD([[makeQuery(id+"F0.imprint","IMPRINT",EDGE,{"derivedFrom":subQ6}),1.0]])]});}
            var Q11;
            {var subQ1=sQuery(id+"F0.wireOp",EDGE,"E136");Q11=makeQuery(id+"F0.imprint","IMPRINT",FACE,{"disambiguationData":[TD([[makeQuery(id+"F0.imprint","IMPRINT",EDGE,{"derivedFrom":subQ1}),-1.0]])]});}
            var Q12;
            {var subQ9=sQuery(id+"F0.wireOp",EDGE,"E46");Q12=makeQuery(id+"F0.imprint","IMPRINT",FACE,{"disambiguationData":[TD([[makeQuery(id+"F0.imprint","IMPRINT",EDGE,{"derivedFrom":subQ9}),-1.0]])]});}
            var Q13;
            {var subQ7=sQuery(id+"F0.wireOp",EDGE,"E50");var subQ8=sQuery(id+"F0.wireOp",EDGE,"E49");var subQ9=makeQuery(id+"F0.imprint","INTERSECT",VERTEX,{"derivedFrom":[subQ8,subQ7]});Q13=makeQuery(id+"F0.imprint","IMPRINT",FACE,{"disambiguationData":[TD([[makeQuery(id+"F0.imprint","IMPRINT",EDGE,{"disambiguationData":[TD([[subQ9,1.0]])],"derivedFrom":subQ8}),-1.0]])]});}
            var Q14;
            {var subQ7=sQuery(id+"F0.wireOp",EDGE,"E140");var subQ8=sQuery(id+"F0.wireOp",EDGE,"E139");var subQ9=makeQuery(id+"F0.imprint","INTERSECT",VERTEX,{"derivedFrom":[subQ8,subQ7]});Q14=makeQuery(id+"F0.imprint","IMPRINT",FACE,{"disambiguationData":[TD([[makeQuery(id+"F0.imprint","IMPRINT",EDGE,{"disambiguationData":[TD([[subQ9,1.0]])],"derivedFrom":subQ8}),-1.0]])]});}
            var Q15;
            {var subQ12=sQuery(id+"F0.wireOp",EDGE,"E336");Q15=makeQuery(id+"F0.imprint","IMPRINT",FACE,{"disambiguationData":[TD([[makeQuery(id+"F0.imprint","IMPRINT",EDGE,{"derivedFrom":subQ12}),1.0]])]});}
            var Q16;
            {var subQ6=sQuery(id+"F0.wireOp",EDGE,"E275");var subQ9=sQuery(id+"F0.wireOp",EDGE,"E274");var subQ10=makeQuery(id+"F0.imprint","INTERSECT",VERTEX,{"derivedFrom":[subQ9,subQ6]});Q16=makeQuery(id+"F0.imprint","IMPRINT",FACE,{"disambiguationData":[TD([[makeQuery(id+"F0.imprint","IMPRINT",EDGE,{"disambiguationData":[TD([[subQ10,1.0]])],"derivedFrom":subQ9}),-1.0]])]});}
            var Q17;
            {var subQ9=sQuery(id+"F0.wireOp",EDGE,"E95");var subQ10=sQuery(id+"F0.wireOp",EDGE,"E94");var subQ11=makeQuery(id+"F0.imprint","INTERSECT",VERTEX,{"derivedFrom":[subQ10,subQ9]});Q17=makeQuery(id+"F0.imprint","IMPRINT",FACE,{"disambiguationData":[TD([[makeQuery(id+"F0.imprint","IMPRINT",EDGE,{"disambiguationData":[TD([[subQ11,1.0]])],"derivedFrom":subQ10}),-1.0]])]});}
            var Q18;
            {var subQ7=sQuery(id+"F0.wireOp",EDGE,"E185");var subQ8=sQuery(id+"F0.wireOp",EDGE,"E184");var subQ9=makeQuery(id+"F0.imprint","INTERSECT",VERTEX,{"derivedFrom":[subQ8,subQ7]});Q18=makeQuery(id+"F0.imprint","IMPRINT",FACE,{"disambiguationData":[TD([[makeQuery(id+"F0.imprint","IMPRINT",EDGE,{"disambiguationData":[TD([[subQ9,1.0]])],"derivedFrom":subQ8}),-1.0]])]});}
            extrude(context, id + "F6", {"entities" : qUnion([Q0, Q1, Q2, Q3, Q4, Q5, Q6, Q7, Q8, Q9, Q10, Q11, Q12, Q13, Q14, Q15, Q16, Q17, Q18]), "depth" : 3.17 * mm});
        }
    });
